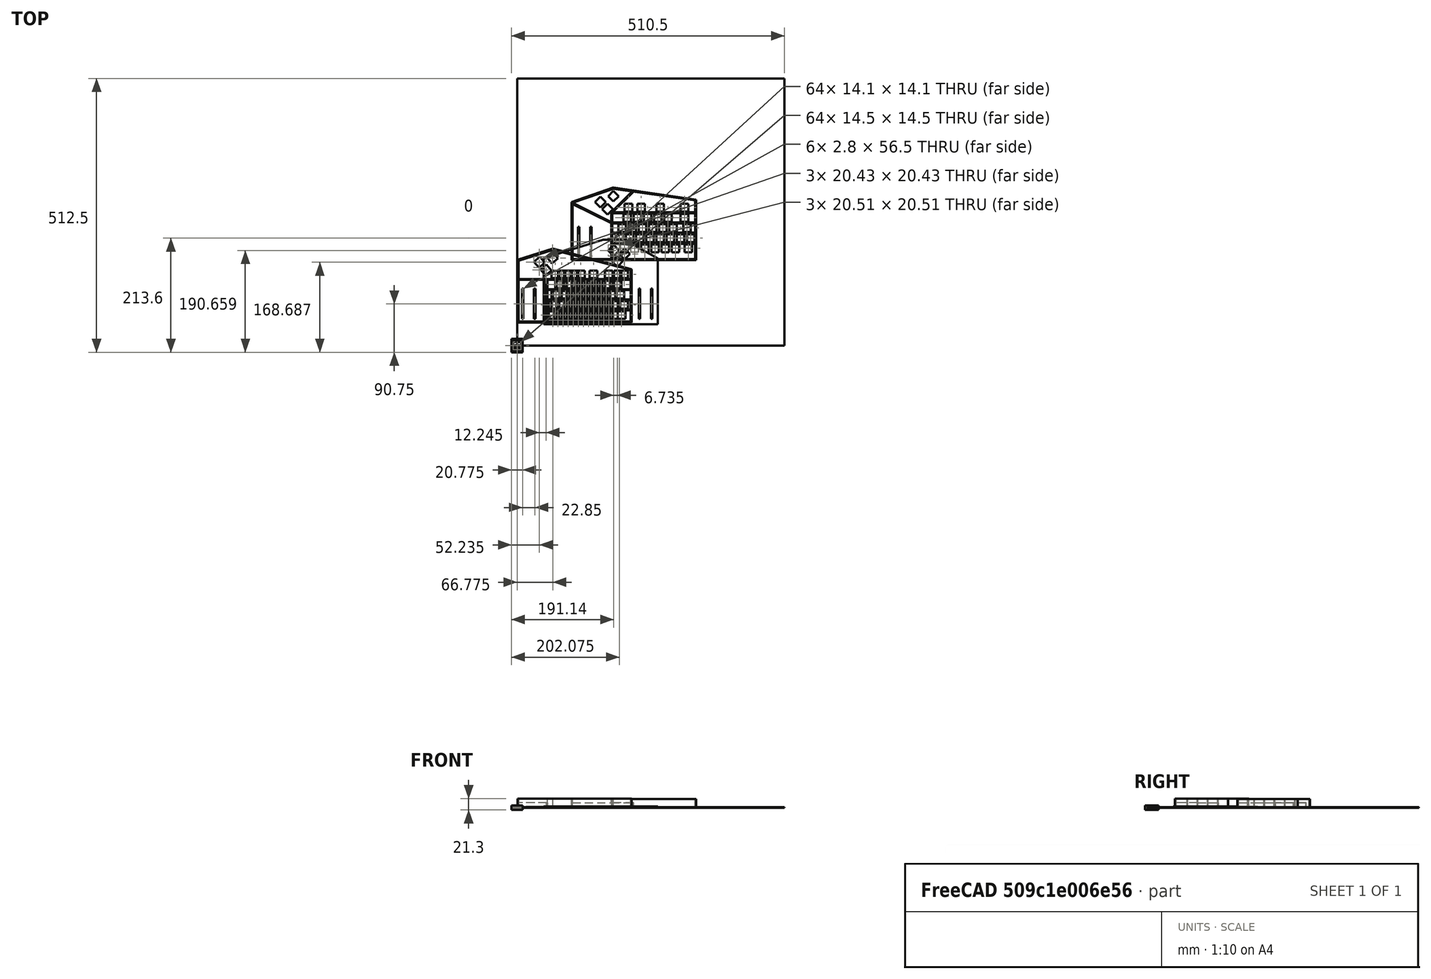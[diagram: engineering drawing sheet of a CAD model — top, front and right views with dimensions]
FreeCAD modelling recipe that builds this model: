
FCSTD DOCUMENT  (FreeCAD 0.22R35869 (Git))
Label: keyboard
License: All rights reserved
LicenseURL: http://en.wikipedia.org/wiki/All_rights_reserved
objects: PartDesign::Pad×30, Sketcher::SketchObject×29, PartDesign::Pocket×23, PartDesign::CoordinateSystem×11, PartDesign::Body×7, Part::Feature×7, App::Part×4, App::DocumentObjectGroup×3, App::Link×3, Mesh::Feature×3, Part::Refine×3, PartDesign::FeatureBase×3, PartDesign::Chamfer×2, PartDesign::Fillet×2, PartDesign::LinearPattern×2, App::FeaturePython×1, Spreadsheet::Sheet×1
note: 176 computed .brp shape members not serialized (recipe doc carries the construction recipe); baked Part::Feature solids carry a one-line shape summary decoded from their .brp

FEATURE [Sketcher::SketchObject] Sketch
  FullyConstrained = true
  MapMode = 5
  Support = -> [XY_Plane001]
  sketch-geometry (8):
    g0: LineSegment StartX=-7.5 StartY=7.5 StartZ=0 EndX=7.5 EndY=7.5 EndZ=0
    g1: LineSegment StartX=7.5 StartY=7.5 StartZ=0 EndX=7.5 EndY=-7.5 EndZ=0
    g2: LineSegment StartX=7.5 StartY=-7.5 StartZ=0 EndX=-7.5 EndY=-7.5 EndZ=0
    g3: LineSegment StartX=-7.5 StartY=-7.5 StartZ=0 EndX=-7.5 EndY=7.5 EndZ=0
    g4: LineSegment StartX=-10.5 StartY=10.5 StartZ=0 EndX=10.5 EndY=10.5 EndZ=0
    g5: LineSegment StartX=10.5 StartY=10.5 StartZ=0 EndX=10.5 EndY=-10.5 EndZ=0
    g6: LineSegment StartX=10.5 StartY=-10.5 StartZ=0 EndX=-10.5 EndY=-10.5 EndZ=0
    g7: LineSegment StartX=-10.5 StartY=-10.5 StartZ=0 EndX=-10.5 EndY=10.5 EndZ=0
  constraints (20):
    c: Coincident(g0,g1)
    c: Coincident(g1,g2)
    c: Coincident(g2,g3)
    c: Coincident(g3,g0)
    c: Horizontal(g2)
    c: Vertical(g1)
    c: Symmetric(g0,g0,g-2)
    c: Symmetric(g0,g2,g-1)
    c: Equal(g0,g3)
    c: DistanceX(g0,g0) = 15
    c: Coincident(g4,g5)
    c: Coincident(g5,g6)
    c: Coincident(g6,g7)
    c: Coincident(g7,g4)
    c: Horizontal(g6)
    c: Vertical(g5)
    c: Symmetric(g4,g4,g-2)
    c: Symmetric(g4,g6,g-1)
    c: Equal(g4,g7)
    c: DistanceX(g4,g0) = 3
FEATURE [PartDesign::Pad] Pad
  Direction = (0,0,1)
  Length = 2.5
  Length2 = 10
  Profile = -> Sketch
  ReferenceAxis = -> Sketch [N_Axis]
  Type = 0
FEATURE [Sketcher::SketchObject] Sketch001
  ExternalGeometry = -> [Pad]
  FullyConstrained = true
  MapMode = 5
  Placement = pos=(0,0,0) rot=(1,0,0;3.14159rad)
  Support = -> [Pad]
  expr: Constraints[11] = 4.15 / 2
  sketch-geometry (5):
    g0: LineSegment StartX=-10.5 StartY=10.5 StartZ=0 EndX=10.5 EndY=10.5 EndZ=0
    g1: LineSegment StartX=10.5 StartY=10.5 StartZ=0 EndX=10.5 EndY=-10.5 EndZ=0
    g2: LineSegment StartX=10.5 StartY=-10.5 StartZ=0 EndX=-10.5 EndY=-10.5 EndZ=0
    g3: LineSegment StartX=-10.5 StartY=-10.5 StartZ=0 EndX=-10.5 EndY=10.5 EndZ=0
    g4: Circle CenterX=0 CenterY=0 CenterZ=0 NormalX=0 NormalY=0 NormalZ=1 AngleXU=0 Radius=2.075
  constraints (12):
    c: Coincident(g0,g1)
    c: Coincident(g1,g2)
    c: Coincident(g2,g3)
    c: Coincident(g3,g0)
    c: Horizontal(g0)
    c: Horizontal(g2)
    c: Vertical(g1)
    c: Vertical(g3)
    c: Coincident(g0,g-3)
    c: Coincident(g1,g-4)
    c: Coincident(g4,g-1)
    c: Radius(g4) = 2.075
FEATURE [PartDesign::Pad] Pad001
  BaseFeature = -> Pad
  Direction = (0,0,-1)
  Length = 4
  Length2 = 10
  Profile = -> Sketch001
  ReferenceAxis = -> Sketch001 [N_Axis]
  Type = 0
FEATURE [Sketcher::SketchObject] Sketch002
  ExternalGeometry = -> [Pad001]
  FullyConstrained = true
  MapMode = 5
  Placement = pos=(0,0,2.5) rot=(0,0,1;0rad)
  Support = -> [Pad001]
  sketch-geometry (8):
    g0: LineSegment StartX=-10.5 StartY=10.5 StartZ=0 EndX=10.5 EndY=10.5 EndZ=0
    g1: LineSegment StartX=10.5 StartY=10.5 StartZ=0 EndX=10.5 EndY=-10.5 EndZ=0
    g2: LineSegment StartX=10.5 StartY=-10.5 StartZ=0 EndX=-10.5 EndY=-10.5 EndZ=0
    g3: LineSegment StartX=-10.5 StartY=-10.5 StartZ=0 EndX=-10.5 EndY=10.5 EndZ=0
    g4: LineSegment StartX=-7.25 StartY=7.25 StartZ=0 EndX=7.25 EndY=7.25 EndZ=0
    g5: LineSegment StartX=7.25 StartY=7.25 StartZ=0 EndX=7.25 EndY=-7.25 EndZ=0
    g6: LineSegment StartX=7.25 StartY=-7.25 StartZ=0 EndX=-7.25 EndY=-7.25 EndZ=0
    g7: LineSegment StartX=-7.25 StartY=-7.25 StartZ=0 EndX=-7.25 EndY=7.25 EndZ=0
  constraints (20):
    c: Coincident(g0,g1)
    c: Coincident(g1,g2)
    c: Coincident(g2,g3)
    c: Coincident(g3,g0)
    c: Horizontal(g0)
    c: Horizontal(g2)
    c: Vertical(g1)
    c: Vertical(g3)
    c: Coincident(g0,g-3)
    c: Coincident(g1,g-4)
    c: Coincident(g4,g5)
    c: Coincident(g5,g6)
    c: Coincident(g6,g7)
    c: Coincident(g7,g4)
    c: Horizontal(g6)
    c: Vertical(g5)
    c: Symmetric(g4,g4,g-2)
    c: Symmetric(g4,g6,g-1)
    c: DistanceX(g4,g4) = 14.5
    c: Equal(g7,g4)
FEATURE [PartDesign::Pad] Pad002
  BaseFeature = -> Pad001
  Direction = (0,0,1)
  Length = 2.3
  Length2 = 10
  Profile = -> Sketch002
  ReferenceAxis = -> Sketch002 [N_Axis]
  Type = 0
FEATURE [PartDesign::Chamfer] Chamfer
  Angle = 45
  Base = -> Pad002 [Edge19,Edge23,Edge11,Edge12]
  BaseFeature = -> Pad002
  ChamferType = 0
  FlipDirection = false
  Size = 3
  Size2 = 1
  SupportTransform = false
  UseAllEdges = false
FEATURE [Sketcher::SketchObject] Sketch003
  FullyConstrained = true
  MapMode = 5
  Placement = pos=(0,0,-4) rot=(1,0,0;3.14159rad)
  Support = -> [Chamfer]
  sketch-geometry (2):
    g0: Circle CenterX=4 CenterY=2.85 CenterZ=0 NormalX=0 NormalY=0 NormalZ=1 AngleXU=0 Radius=0.75
    g1: Circle CenterX=-2.9 CenterY=5 CenterZ=0 NormalX=0 NormalY=0 NormalZ=1 AngleXU=0 Radius=0.75
  constraints (6):
    c: DistanceX(g-1,g0) = 4
    c: DistanceY(g-1,g0) = 2.85
    c: Radius(g0) = 0.75
    c: DistanceX(g1,g-1) = 2.9
    c: DistanceY(g-1,g1) = 5
    c: Equal(g1,g0)
FEATURE [PartDesign::Pocket] Pocket
  BaseFeature = -> Chamfer
  Direction = (0,0,1)
  Length = 5
  Length2 = 5
  Profile = -> Sketch003
  ReferenceAxis = -> Sketch003 [N_Axis]
  Type = 1
FEATURE [PartDesign::Chamfer] Chamfer001
  Angle = 45
  Base = -> Pocket [Edge27,Edge26]
  BaseFeature = -> Pocket
  ChamferType = 1
  FlipDirection = false
  Size = 1.8
  Size2 = 3.999
  SupportTransform = false
  UseAllEdges = false
FEATURE [PartDesign::Body] Body
  Group = -> [Sketch,Pad,Sketch001,Pad001,Sketch002,Pad002,Chamfer,Sketch003,Pocket,Chamfer001]
  Origin = -> Origin001
  Tip = -> Chamfer001
FEATURE [Sketcher::SketchObject] Sketch004
  FullyConstrained = true
  MapMode = 5
  Support = -> [XY_Plane002]
  sketch-geometry (8):
    g0: LineSegment StartX=-7.5 StartY=7.5 StartZ=0 EndX=7.5 EndY=7.5 EndZ=0
    g1: LineSegment StartX=7.5 StartY=7.5 StartZ=0 EndX=7.5 EndY=-7.5 EndZ=0
    g2: LineSegment StartX=7.5 StartY=-7.5 StartZ=0 EndX=-7.5 EndY=-7.5 EndZ=0
    g3: LineSegment StartX=-7.5 StartY=-7.5 StartZ=0 EndX=-7.5 EndY=7.5 EndZ=0
    g4: LineSegment StartX=-10.5 StartY=10.5 StartZ=0 EndX=10.5 EndY=10.5 EndZ=0
    g5: LineSegment StartX=10.5 StartY=10.5 StartZ=0 EndX=10.5 EndY=-10.5 EndZ=0
    g6: LineSegment StartX=10.5 StartY=-10.5 StartZ=0 EndX=-10.5 EndY=-10.5 EndZ=0
    g7: LineSegment StartX=-10.5 StartY=-10.5 StartZ=0 EndX=-10.5 EndY=10.5 EndZ=0
  constraints (20):
    c: Coincident(g0,g1)
    c: Coincident(g1,g2)
    c: Coincident(g2,g3)
    c: Coincident(g3,g0)
    c: Horizontal(g2)
    c: Vertical(g1)
    c: Symmetric(g0,g0,g-2)
    c: Symmetric(g0,g2,g-1)
    c: Equal(g0,g3)
    c: DistanceX(g0,g0) = 15
    c: Coincident(g4,g5)
    c: Coincident(g5,g6)
    c: Coincident(g6,g7)
    c: Coincident(g7,g4)
    c: Horizontal(g6)
    c: Vertical(g5)
    c: Symmetric(g4,g4,g-2)
    c: Symmetric(g4,g6,g-1)
    c: Equal(g4,g7)
    c: DistanceX(g4,g0) = 3
FEATURE [PartDesign::Pad] Pad003
  Direction = (0,0,1)
  Length = 2.5
  Length2 = 10
  Profile = -> Sketch004
  ReferenceAxis = -> Sketch004 [N_Axis]
  Type = 0
FEATURE [Sketcher::SketchObject] Sketch005
  ExternalGeometry = -> [Pad003]
  FullyConstrained = true
  MapMode = 5
  Placement = pos=(0,0,0) rot=(1,0,0;3.14159rad)
  Support = -> [Pad003]
  expr: Constraints[11] = 4.15 / 2
  sketch-geometry (5):
    g0: LineSegment StartX=-10.5 StartY=10.5 StartZ=0 EndX=10.5 EndY=10.5 EndZ=0
    g1: LineSegment StartX=10.5 StartY=10.5 StartZ=0 EndX=10.5 EndY=-10.5 EndZ=0
    g2: LineSegment StartX=10.5 StartY=-10.5 StartZ=0 EndX=-10.5 EndY=-10.5 EndZ=0
    g3: LineSegment StartX=-10.5 StartY=-10.5 StartZ=0 EndX=-10.5 EndY=10.5 EndZ=0
    g4: Circle CenterX=0 CenterY=0 CenterZ=0 NormalX=0 NormalY=0 NormalZ=1 AngleXU=0 Radius=2.075
  constraints (12):
    c: Coincident(g0,g1)
    c: Coincident(g1,g2)
    c: Coincident(g2,g3)
    c: Coincident(g3,g0)
    c: Horizontal(g0)
    c: Horizontal(g2)
    c: Vertical(g1)
    c: Vertical(g3)
    c: Coincident(g0,g-3)
    c: Coincident(g1,g-4)
    c: Coincident(g4,g-1)
    c: Radius(g4) = 2.075
FEATURE [PartDesign::Pad] Pad004
  BaseFeature = -> Pad003
  Direction = (0,0,-1)
  Length = 4
  Length2 = 10
  Profile = -> Sketch005
  ReferenceAxis = -> Sketch005 [N_Axis]
  Type = 0
FEATURE [Sketcher::SketchObject] Sketch006
  ExternalGeometry = -> [Pad004]
  FullyConstrained = true
  MapMode = 5
  Placement = pos=(0,0,2.5) rot=(0,0,1;0rad)
  Support = -> [Pad004]
  sketch-geometry (8):
    g0: LineSegment StartX=-10.5 StartY=10.5 StartZ=0 EndX=10.5 EndY=10.5 EndZ=0
    g1: LineSegment StartX=10.5 StartY=10.5 StartZ=0 EndX=10.5 EndY=-10.5 EndZ=0
    g2: LineSegment StartX=10.5 StartY=-10.5 StartZ=0 EndX=-10.5 EndY=-10.5 EndZ=0
    g3: LineSegment StartX=-10.5 StartY=-10.5 StartZ=0 EndX=-10.5 EndY=10.5 EndZ=0
    g4: LineSegment StartX=-7.25 StartY=7.25 StartZ=0 EndX=7.25 EndY=7.25 EndZ=0
    g5: LineSegment StartX=7.25 StartY=7.25 StartZ=0 EndX=7.25 EndY=-7.25 EndZ=0
    g6: LineSegment StartX=7.25 StartY=-7.25 StartZ=0 EndX=-7.25 EndY=-7.25 EndZ=0
    g7: LineSegment StartX=-7.25 StartY=-7.25 StartZ=0 EndX=-7.25 EndY=7.25 EndZ=0
  constraints (20):
    c: Coincident(g0,g1)
    c: Coincident(g1,g2)
    c: Coincident(g2,g3)
    c: Coincident(g3,g0)
    c: Horizontal(g0)
    c: Horizontal(g2)
    c: Vertical(g1)
    c: Vertical(g3)
    c: Coincident(g0,g-3)
    c: Coincident(g1,g-4)
    c: Coincident(g4,g5)
    c: Coincident(g5,g6)
    c: Coincident(g6,g7)
    c: Coincident(g7,g4)
    c: Horizontal(g6)
    c: Vertical(g5)
    c: Symmetric(g4,g4,g-2)
    c: Symmetric(g4,g6,g-1)
    c: DistanceX(g4,g4) = 14.5
    c: Equal(g7,g4)
FEATURE [PartDesign::Pad] Pad005
  BaseFeature = -> Pad004
  Direction = (0,0,1)
  Length = 2.3
  Length2 = 10
  Profile = -> Sketch006
  ReferenceAxis = -> Sketch006 [N_Axis]
  Type = 0
FEATURE [Sketcher::SketchObject] Sketch007
  ExternalGeometry = -> [Pad005]
  FullyConstrained = true
  MapMode = 5
  Placement = pos=(0,0,-4) rot=(1,0,0;3.14159rad)
  Support = -> [Pad005]
  sketch-geometry (22):
    g0: LineSegment StartX=-7.5 StartY=6.5 StartZ=0 EndX=-2 EndY=6.5 EndZ=0
    g1: LineSegment StartX=-2 StartY=6.5 StartZ=0 EndX=-2 EndY=3.5 EndZ=0
    g2: LineSegment StartX=-2 StartY=3.5 StartZ=0 EndX=-7.5 EndY=3.5 EndZ=0
    g3: LineSegment StartX=-7.5 StartY=3.5 StartZ=0 EndX=-7.5 EndY=6.5 EndZ=0
    g4: LineSegment StartX=3 StartY=4.35 StartZ=0 EndX=7.5 EndY=4.35 EndZ=0
    g5: LineSegment StartX=7.5 StartY=4.35 StartZ=0 EndX=7.5 EndY=1.35 EndZ=0
    g6: LineSegment StartX=7.5 StartY=1.35 StartZ=0 EndX=3 EndY=1.35 EndZ=0
    g7: LineSegment StartX=3 StartY=1.35 StartZ=0 EndX=3 EndY=4.35 EndZ=0
    g8: Circle CenterX=-2.9 CenterY=5 CenterZ=0 NormalX=0 NormalY=0 NormalZ=1 AngleXU=0 Radius=0.75
    g9: Circle CenterX=4 CenterY=2.85 CenterZ=0 NormalX=0 NormalY=0 NormalZ=1 AngleXU=0 Radius=0.75
    g10: LineSegment StartX=-2.9 StartY=5 StartZ=0 EndX=-7.5 EndY=5 EndZ=0
    g11: LineSegment StartX=-7.5 StartY=5 StartZ=0 EndX=-7.5 EndY=6.5 EndZ=0
    g12: LineSegment StartX=-7.5 StartY=5 StartZ=0 EndX=-7.5 EndY=3.5 EndZ=0
    g13: LineSegment StartX=4 StartY=2.85 StartZ=0 EndX=7.5 EndY=2.85 EndZ=0
    g14: LineSegment StartX=7.5 StartY=2.85 StartZ=0 EndX=7.5 EndY=1.35 EndZ=0
    g15: LineSegment StartX=7.5 StartY=2.85 StartZ=0 EndX=7.5 EndY=4.35 EndZ=0
    g16: LineSegment StartX=3 StartY=4.35 StartZ=0 EndX=3.8 EndY=3.57284 EndZ=0
    g17: LineSegment StartX=3 StartY=1.35 StartZ=0 EndX=3.8 EndY=2.12716 EndZ=0
    g18: ArcOfCircle CenterX=4 CenterY=2.85 CenterZ=0 NormalX=0 NormalY=0 NormalZ=1 AngleXU=0 Radius=0.75 StartAngle=1.84073 EndAngle=4.44246
    g19: LineSegment StartX=-2 StartY=6.5 StartZ=0 EndX=-2.7 EndY=5.72284 EndZ=0
    g20: LineSegment StartX=-2 StartY=3.5 StartZ=0 EndX=-2.7 EndY=4.27716 EndZ=0
    g21: ArcOfCircle CenterX=-2.9 CenterY=5 CenterZ=0 NormalX=0 NormalY=0 NormalZ=1 AngleXU=0 Radius=0.75 StartAngle=4.98232 EndAngle=7.58405
  constraints (60):
    c: Coincident(g0,g1)
    c: Coincident(g1,g2)
    c: Coincident(g2,g3)
    c: Coincident(g3,g0)
    c: Horizontal(g0)
    c: Horizontal(g2)
    c: Vertical(g1)
    c: Vertical(g3)
    c: Coincident(g4,g5)
    c: Coincident(g5,g6)
    c: Coincident(g6,g7)
    c: Coincident(g7,g4)
    c: Horizontal(g4)
    c: Horizontal(g6)
    c: Vertical(g5)
    c: Vertical(g7)
    c: PointOnObject(g4,g-4)
    c: PointOnObject(g0,g-3)
    c: DistanceY(g-1,g9) = 2.85
    c: DistanceX(g-1,g9) = 4
    c: Radius(g9) = 0.75
    c: DistanceY(g-1,g8) = 5
    c: DistanceX(g8,g-1) = 2.9
    c: Radius(g8) = 0.75
    c: Coincident(g10,g8)
    c: PointOnObject(g10,g-3)
    c: Coincident(g11,g10)
    c: Equal(g12,g11)
    c: Coincident(g12,g10)
    c: Horizontal(g10)
    c: Coincident(g12,g2)
    c: Coincident(g11,g0)
    c: Coincident(g13,g9)
    c: PointOnObject(g13,g-4)
    c: Coincident(g14,g13)
    c: Coincident(g15,g13)
    c: Equal(g15,g14)
    c: Horizontal(g13)
    c: Coincident(g15,g4)
    c: Coincident(g14,g5)
    c: DistanceX(g6,g5) = 4.5
    c: DistanceX(g2,g2) = 5.5
    c: DistanceY(g1,g1) = 3
    c: Coincident(g16,g4)
    c: Coincident(g17,g6)
    c: Coincident(g18,g9)
    c: Coincident(g18,g16)
    c: Coincident(g18,g17)
    c: Equal(g18,g9)
    c: DistanceX(g17,g18) = 0.2
    c: Equal(g16,g17)
    c: Coincident(g19,g0)
    c: PointOnObject(g19,g8)
    c: Coincident(g20,g2)
    c: Coincident(g21,g8)
    c: Coincident(g21,g19)
    c: Coincident(g21,g20)
    c: Equal(g19,g20)
    c: DistanceX(g21,g20) = 0.2
    c: Equal(g1,g7)
FEATURE [PartDesign::Pocket] Pocket001
  BaseFeature = -> Pad005
  Direction = (0,0,1)
  Length = 0
  Length2 = 5
  Profile = -> Sketch007
  ReferenceAxis = -> Sketch007 [N_Axis]
  Type = 3
  UpToFace = -> Pad005 [Face20]
FEATURE [PartDesign::Fillet] Fillet
  Base = -> Pocket001 [Edge65,Edge68,Edge49,Edge53]
  BaseFeature = -> Pocket001
  Radius = 1
  SupportTransform = false
  UseAllEdges = false
FEATURE [Sketcher::SketchObject] Sketch008
  ExternalGeometry = -> [Fillet]
  FullyConstrained = true
  MapMode = 5
  Placement = pos=(0,0,4.8) rot=(0,0,1;0rad)
  Support = -> [Fillet]
  sketch-geometry (4):
    g0: LineSegment StartX=-10.5 StartY=0 StartZ=0 EndX=10.5 EndY=0 EndZ=0
    g1: LineSegment StartX=10.5 StartY=0 StartZ=0 EndX=10.5 EndY=-6.5 EndZ=0
    g2: LineSegment StartX=10.5 StartY=-6.5 StartZ=0 EndX=-10.5 EndY=-6.5 EndZ=0
    g3: LineSegment StartX=-10.5 StartY=-6.5 StartZ=0 EndX=-10.5 EndY=0 EndZ=0
  constraints (11):
    c: Coincident(g0,g1)
    c: Coincident(g1,g2)
    c: Coincident(g2,g3)
    c: Coincident(g3,g0)
    c: Horizontal(g2)
    c: Vertical(g1)
    c: Vertical(g3)
    c: PointOnObject(g0,g-1)
    c: PointOnObject(g2,g-3)
    c: Symmetric(g0,g0,g-2)
    c: PointOnObject(g2,g-4)
FEATURE [PartDesign::Pocket] Pocket002
  BaseFeature = -> Fillet
  Direction = (0,0,-1)
  Length = 0
  Length2 = 5
  Profile = -> Sketch008
  ReferenceAxis = -> Sketch008 [N_Axis]
  Type = 3
  UpToFace = -> Fillet [Face23]
FEATURE [PartDesign::Pad] Pad006
  BaseFeature = -> Pocket002
  Direction = (0,-1,0)
  Length = 2
  Length2 = 10
  Profile = -> Pocket002 [Face10,Face26,Face39]
  Type = 0
FEATURE [PartDesign::Pad] Pad007
  BaseFeature = -> Pad006
  Direction = (0,1,0)
  Length = 2
  Length2 = 10
  Profile = -> Pad006 [Face13,Face34,Face50]
  Type = 0
FEATURE [PartDesign::CoordinateSystem] LCS_Origin
  AttacherType = Attacher::AttachEngine3D
  MapMode = 2
  Support = -> [X_Axis006]
FEATURE [App::DocumentObjectGroup] Constraints
FEATURE [App::FeaturePython] Variables  # WARN: FeaturePython — macro-defined, semantics opaque (R4)
  Type = App::PropertyContainer
FEATURE [App::DocumentObjectGroup] Configurations
FEATURE [PartDesign::CoordinateSystem] LCS_0
  AttacherType = Attacher::AttachEngine3D
  MapMode = 2
  Support = -> [X_Axis007]
FEATURE [Sketcher::SketchObject] Sketch013
  FullyConstrained = true
  MapMode = 5
  Support = -> [XY_Plane008]
  sketch-geometry (6):
    g0: ArcOfCircle CenterX=-0.866025 CenterY=0 CenterZ=0 NormalX=0 NormalY=0 NormalZ=1 AngleXU=0 Radius=1 StartAngle=5.75959 EndAngle=6.80678
    g1: LineSegment StartX=0 StartY=0.5 StartZ=0 EndX=0 EndY=1 EndZ=0
    g2: LineSegment StartX=0 StartY=1 StartZ=0 EndX=1 EndY=1 EndZ=0
    g3: LineSegment StartX=1 StartY=1 StartZ=0 EndX=1 EndY=-1 EndZ=0
    g4: LineSegment StartX=1 StartY=-1 StartZ=0 EndX=0 EndY=-1 EndZ=0
    g5: LineSegment StartX=0 StartY=-1 StartZ=0 EndX=2e-16 EndY=-0.5 EndZ=0
  constraints (19):
    c: PointOnObject(g0,g-1)
    c: PointOnObject(g0,g-2)
    c: PointOnObject(g0,g-2)
    c: Coincident(g1,g2)
    c: Horizontal(g2)
    c: Coincident(g2,g3)
    c: Coincident(g3,g4)
    c: PointOnObject(g4,g-2)
    c: Horizontal(g4)
    c: Coincident(g4,g5)
    c: Coincident(g5,g0)
    c: PointOnObject(g1,g-2)
    c: Vertical(g3)
    c: DistanceY(g3,g3) = 2
    c: Radius(g0) = 1
    c: Coincident(g1,g0)
    c: Equal(g1,g5)
    c: DistanceY(g0,g0) = 1
    c: DistanceX(g2,g2) = 1
FEATURE [PartDesign::Pad] Pad011
  Direction = (0,0,1)
  Length = 4
  Length2 = 10
  Profile = -> Sketch013
  ReferenceAxis = -> Sketch013 [N_Axis]
  Reversed = true
  Type = 0
FEATURE [PartDesign::CoordinateSystem] Local_CS
  AttacherType = Attacher::AttachEngine3D
  MapMode = 45
  Placement = pos=(3.31163,-2.85,0) rot=(0,0.707107,0.707107;3.14159rad)
  Support = -> [Pad007]
FEATURE [PartDesign::CoordinateSystem] Local_CS001
  AttacherType = Attacher::AttachEngine3D
  MapMode = 45
  Placement = pos=(-2.22398,-5,0) rot=(0,0.707107,0.707107;3.14159rad)
  Support = -> [Pad007]
FEATURE [PartDesign::Body] Body001
  Group = -> [Sketch004,Pad003,Sketch005,Pad004,Sketch006,Pad005,Sketch007,Pocket001,Fillet,Sketch008,Pocket002,Pad006,Pad007,Local_CS,Local_CS001]
  Origin = -> Origin002
  Tip = -> Pad007
FEATURE [Sketcher::SketchObject] Sketch014
  ExternalGeometry = -> [Pad011]
  FullyConstrained = true
  MapMode = 5
  Support = -> [XY_Plane008]
  sketch-geometry (21):
    g0: LineSegment StartX=1 StartY=1 StartZ=0 EndX=1.66667 EndY=-0.8 EndZ=0
    g1: LineSegment StartX=1.66667 StartY=-0.8 StartZ=0 EndX=2.33333 EndY=1 EndZ=0
    g2: LineSegment StartX=2.33333 StartY=1 StartZ=0 EndX=3 EndY=-0.8 EndZ=0
    g3: LineSegment StartX=3 StartY=-0.8 StartZ=0 EndX=3.66667 EndY=1 EndZ=0
    g4: LineSegment StartX=3.66667 StartY=1 StartZ=0 EndX=4.33333 EndY=-0.8 EndZ=0
    g5: LineSegment StartX=4.33333 StartY=-0.8 StartZ=0 EndX=5 EndY=1 EndZ=0
    g6: LineSegment StartX=1 StartY=1 StartZ=0 EndX=5 EndY=1 EndZ=0
    g7: LineSegment StartX=1 StartY=-1 StartZ=0 EndX=4.33333 EndY=-1 EndZ=0
    g8: LineSegment StartX=1 StartY=0.8 StartZ=0 EndX=1.66667 EndY=-1 EndZ=0
    g9: LineSegment StartX=1.66667 StartY=-1 StartZ=0 EndX=2.33333 EndY=0.8 EndZ=0
    g10: LineSegment StartX=2.33333 StartY=0.8 StartZ=0 EndX=3 EndY=-1 EndZ=0
    g11: LineSegment StartX=3 StartY=-1 StartZ=0 EndX=3.66667 EndY=0.8 EndZ=0
    g12: LineSegment StartX=3.66667 StartY=0.8 StartZ=0 EndX=4.33333 EndY=-1 EndZ=0
    g13: LineSegment StartX=4.33333 StartY=-1 StartZ=0 EndX=5 EndY=0.8 EndZ=0
    g14: LineSegment StartX=1.66667 StartY=-0.8 StartZ=0 EndX=1.66667 EndY=-1 EndZ=0
    g15: LineSegment StartX=3 StartY=-0.8 StartZ=0 EndX=3 EndY=-1 EndZ=0
    g16: LineSegment StartX=2.33333 StartY=0.8 StartZ=0 EndX=2.33333 EndY=1 EndZ=0
    g17: LineSegment StartX=3.66667 StartY=0.8 StartZ=0 EndX=3.66667 EndY=1 EndZ=0
    g18: LineSegment StartX=5 StartY=0.8 StartZ=0 EndX=5 EndY=1 EndZ=0
    g19: LineSegment StartX=4.33333 StartY=-0.8 StartZ=0 EndX=4.33333 EndY=-1 EndZ=0
    g20: LineSegment StartX=1 StartY=0.8 StartZ=0 EndX=1 EndY=1 EndZ=0
  constraints (55):
    c: Coincident(g-3,g0)
    c: Coincident(g0,g1)
    c: Coincident(g1,g2)
    c: Coincident(g2,g3)
    c: Coincident(g3,g4)
    c: Coincident(g6,g0)
    c: Coincident(g6,g5)
    c: Coincident(g7,g-3)
    c: Horizontal(g7)
    c: Horizontal(g6)
    c: PointOnObject(g3,g6)
    c: PointOnObject(g1,g6)
    c: Coincident(g5,g4)
    c: PointOnObject(g8,g-3)
    c: PointOnObject(g8,g7)
    c: Coincident(g8,g9)
    c: Coincident(g9,g10)
    c: PointOnObject(g10,g7)
    c: Coincident(g10,g11)
    c: Coincident(g11,g12)
    c: Coincident(g12,g7)
    c: Coincident(g12,g13)
    c: Coincident(g14,g0)
    c: Coincident(g14,g8)
    c: Coincident(g15,g2)
    c: Coincident(g15,g10)
    c: Coincident(g16,g9)
    c: Coincident(g16,g1)
    c: Coincident(g17,g11)
    c: Coincident(g17,g3)
    c: Vertical(g17)
    c: Coincident(g18,g13)
    c: Coincident(g18,g5)
    c: Coincident(g19,g4)
    c: Coincident(g19,g12)
    c: Equal(g14,g16)
    c: Equal(g16,g15)
    c: Equal(g15,g17)
    c: Equal(g17,g19)
    c: Equal(g19,g18)
    c: Vertical(g14)
    c: Vertical(g16)
    c: Vertical(g15)
    c: Vertical(g18)
    c: Vertical(g19)
    c: Equal(g0,g1)
    c: Equal(g2,g3)
    c: Equal(g3,g4)
    c: Equal(g4,g5)
    c: Equal(g5,g8)
    c: Equal(g8,g9)
    c: Coincident(g20,g8)
    c: Coincident(g20,g0)
    c: DistanceY(g18,g18) = 0.2
    c: DistanceX(g6,g6) = 4
FEATURE [PartDesign::Pad] Pad012
  BaseFeature = -> Pad011
  Direction = (0,0,1)
  Length = 4
  Length2 = 10
  Profile = -> Sketch014
  ReferenceAxis = -> Sketch014 [N_Axis]
  Reversed = true
  Type = 0
FEATURE [PartDesign::CoordinateSystem] LCS_0002
  AttacherType = Attacher::AttachEngine3D
  MapMode = 2
  Support = -> [X_Axis009]
FEATURE [Sketcher::SketchObject] Sketch015
  FullyConstrained = true
  MapMode = 5
  Support = -> [XY_Plane010]
  sketch-geometry (8):
    g0: LineSegment StartX=-7.5 StartY=7.5 StartZ=0 EndX=7.5 EndY=7.5 EndZ=0
    g1: LineSegment StartX=7.5 StartY=7.5 StartZ=0 EndX=7.5 EndY=-7.5 EndZ=0
    g2: LineSegment StartX=7.5 StartY=-7.5 StartZ=0 EndX=-7.5 EndY=-7.5 EndZ=0
    g3: LineSegment StartX=-7.5 StartY=-7.5 StartZ=0 EndX=-7.5 EndY=7.5 EndZ=0
    g4: LineSegment StartX=-10.5 StartY=10.5 StartZ=0 EndX=10.5 EndY=10.5 EndZ=0
    g5: LineSegment StartX=10.5 StartY=10.5 StartZ=0 EndX=10.5 EndY=-10.5 EndZ=0
    g6: LineSegment StartX=10.5 StartY=-10.5 StartZ=0 EndX=-10.5 EndY=-10.5 EndZ=0
    g7: LineSegment StartX=-10.5 StartY=-10.5 StartZ=0 EndX=-10.5 EndY=10.5 EndZ=0
  constraints (20):
    c: Coincident(g0,g1)
    c: Coincident(g1,g2)
    c: Coincident(g2,g3)
    c: Coincident(g3,g0)
    c: Horizontal(g2)
    c: Vertical(g1)
    c: Symmetric(g0,g0,g-2)
    c: Symmetric(g0,g2,g-1)
    c: Equal(g0,g3)
    c: DistanceX(g0,g0) = 15
    c: Coincident(g4,g5)
    c: Coincident(g5,g6)
    c: Coincident(g6,g7)
    c: Coincident(g7,g4)
    c: Horizontal(g6)
    c: Vertical(g5)
    c: Symmetric(g4,g4,g-2)
    c: Symmetric(g4,g6,g-1)
    c: Equal(g4,g7)
    c: DistanceX(g4,g0) = 3
FEATURE [PartDesign::Pad] Pad013
  Direction = (0,0,1)
  Length = 2.5
  Length2 = 10
  Profile = -> Sketch015
  ReferenceAxis = -> Sketch015 [N_Axis]
  Type = 0
FEATURE [Sketcher::SketchObject] Sketch016
  ExternalGeometry = -> [Pad013]
  FullyConstrained = true
  MapMode = 5
  Placement = pos=(0,0,0) rot=(1,0,0;3.14159rad)
  Support = -> [Pad013]
  expr: Constraints[11] = 4.15 / 2
  sketch-geometry (5):
    g0: LineSegment StartX=-10.5 StartY=10.5 StartZ=0 EndX=10.5 EndY=10.5 EndZ=0
    g1: LineSegment StartX=10.5 StartY=10.5 StartZ=0 EndX=10.5 EndY=-10.5 EndZ=0
    g2: LineSegment StartX=10.5 StartY=-10.5 StartZ=0 EndX=-10.5 EndY=-10.5 EndZ=0
    g3: LineSegment StartX=-10.5 StartY=-10.5 StartZ=0 EndX=-10.5 EndY=10.5 EndZ=0
    g4: Circle CenterX=0 CenterY=0 CenterZ=0 NormalX=0 NormalY=0 NormalZ=1 AngleXU=0 Radius=2.075
  constraints (12):
    c: Coincident(g0,g1)
    c: Coincident(g1,g2)
    c: Coincident(g2,g3)
    c: Coincident(g3,g0)
    c: Horizontal(g0)
    c: Horizontal(g2)
    c: Vertical(g1)
    c: Vertical(g3)
    c: Coincident(g0,g-3)
    c: Coincident(g1,g-4)
    c: Coincident(g4,g-1)
    c: Radius(g4) = 2.075
FEATURE [PartDesign::Pad] Pad014
  BaseFeature = -> Pad013
  Direction = (0,0,-1)
  Length = 4
  Length2 = 10
  Profile = -> Sketch016
  ReferenceAxis = -> Sketch016 [N_Axis]
  Type = 0
FEATURE [Sketcher::SketchObject] Sketch017
  ExternalGeometry = -> [Pad014]
  FullyConstrained = true
  MapMode = 5
  Placement = pos=(0,0,2.5) rot=(0,0,1;0rad)
  Support = -> [Pad014]
  sketch-geometry (8):
    g0: LineSegment StartX=-10.5 StartY=10.5 StartZ=0 EndX=10.5 EndY=10.5 EndZ=0
    g1: LineSegment StartX=10.5 StartY=10.5 StartZ=0 EndX=10.5 EndY=-10.5 EndZ=0
    g2: LineSegment StartX=10.5 StartY=-10.5 StartZ=0 EndX=-10.5 EndY=-10.5 EndZ=0
    g3: LineSegment StartX=-10.5 StartY=-10.5 StartZ=0 EndX=-10.5 EndY=10.5 EndZ=0
    g4: LineSegment StartX=-7.25 StartY=7.25 StartZ=0 EndX=7.25 EndY=7.25 EndZ=0
    g5: LineSegment StartX=7.25 StartY=7.25 StartZ=0 EndX=7.25 EndY=-7.25 EndZ=0
    g6: LineSegment StartX=7.25 StartY=-7.25 StartZ=0 EndX=-7.25 EndY=-7.25 EndZ=0
    g7: LineSegment StartX=-7.25 StartY=-7.25 StartZ=0 EndX=-7.25 EndY=7.25 EndZ=0
  constraints (20):
    c: Coincident(g0,g1)
    c: Coincident(g1,g2)
    c: Coincident(g2,g3)
    c: Coincident(g3,g0)
    c: Horizontal(g0)
    c: Horizontal(g2)
    c: Vertical(g1)
    c: Vertical(g3)
    c: Coincident(g0,g-3)
    c: Coincident(g1,g-4)
    c: Coincident(g4,g5)
    c: Coincident(g5,g6)
    c: Coincident(g6,g7)
    c: Coincident(g7,g4)
    c: Horizontal(g6)
    c: Vertical(g5)
    c: Symmetric(g4,g4,g-2)
    c: Symmetric(g4,g6,g-1)
    c: DistanceX(g4,g4) = 14.5
    c: Equal(g7,g4)
FEATURE [PartDesign::Pad] Pad015
  BaseFeature = -> Pad014
  Direction = (0,0,1)
  Length = 2.3
  Length2 = 10
  Profile = -> Sketch017
  ReferenceAxis = -> Sketch017 [N_Axis]
  Type = 0
FEATURE [Sketcher::SketchObject] Sketch018
  ExternalGeometry = -> [Pad015]
  FullyConstrained = true
  MapMode = 5
  Placement = pos=(0,0,-4) rot=(1,0,0;3.14159rad)
  Support = -> [Pad015]
  sketch-geometry (22):
    g0: LineSegment StartX=-7.5 StartY=6.5 StartZ=0 EndX=-2 EndY=6.5 EndZ=0
    g1: LineSegment StartX=-2 StartY=6.5 StartZ=0 EndX=-2 EndY=3.5 EndZ=0
    g2: LineSegment StartX=-2 StartY=3.5 StartZ=0 EndX=-7.5 EndY=3.5 EndZ=0
    g3: LineSegment StartX=-7.5 StartY=3.5 StartZ=0 EndX=-7.5 EndY=6.5 EndZ=0
    g4: LineSegment StartX=3 StartY=4.35 StartZ=0 EndX=7.5 EndY=4.35 EndZ=0
    g5: LineSegment StartX=7.5 StartY=4.35 StartZ=0 EndX=7.5 EndY=1.35 EndZ=0
    g6: LineSegment StartX=7.5 StartY=1.35 StartZ=0 EndX=3 EndY=1.35 EndZ=0
    g7: LineSegment StartX=3 StartY=1.35 StartZ=0 EndX=3 EndY=4.35 EndZ=0
    g8: Circle CenterX=-2.9 CenterY=5 CenterZ=0 NormalX=0 NormalY=0 NormalZ=1 AngleXU=0 Radius=0.75
    g9: Circle CenterX=4 CenterY=2.85 CenterZ=0 NormalX=0 NormalY=0 NormalZ=1 AngleXU=0 Radius=0.75
    g10: LineSegment StartX=-2.9 StartY=5 StartZ=0 EndX=-7.5 EndY=5 EndZ=0
    g11: LineSegment StartX=-7.5 StartY=5 StartZ=0 EndX=-7.5 EndY=6.5 EndZ=0
    g12: LineSegment StartX=-7.5 StartY=5 StartZ=0 EndX=-7.5 EndY=3.5 EndZ=0
    g13: LineSegment StartX=4 StartY=2.85 StartZ=0 EndX=7.5 EndY=2.85 EndZ=0
    g14: LineSegment StartX=7.5 StartY=2.85 StartZ=0 EndX=7.5 EndY=1.35 EndZ=0
    g15: LineSegment StartX=7.5 StartY=2.85 StartZ=0 EndX=7.5 EndY=4.35 EndZ=0
    g16: LineSegment StartX=3 StartY=4.35 StartZ=0 EndX=3.8 EndY=3.57284 EndZ=0
    g17: LineSegment StartX=3 StartY=1.35 StartZ=0 EndX=3.8 EndY=2.12716 EndZ=0
    g18: ArcOfCircle CenterX=4 CenterY=2.85 CenterZ=0 NormalX=0 NormalY=0 NormalZ=1 AngleXU=0 Radius=0.75 StartAngle=1.84073 EndAngle=4.44246
    g19: LineSegment StartX=-2 StartY=6.5 StartZ=0 EndX=-2.7 EndY=5.72284 EndZ=0
    g20: LineSegment StartX=-2 StartY=3.5 StartZ=0 EndX=-2.7 EndY=4.27716 EndZ=0
    g21: ArcOfCircle CenterX=-2.9 CenterY=5 CenterZ=0 NormalX=0 NormalY=0 NormalZ=1 AngleXU=0 Radius=0.75 StartAngle=4.98232 EndAngle=7.58405
  constraints (60):
    c: Coincident(g0,g1)
    c: Coincident(g1,g2)
    c: Coincident(g2,g3)
    c: Coincident(g3,g0)
    c: Horizontal(g0)
    c: Horizontal(g2)
    c: Vertical(g1)
    c: Vertical(g3)
    c: Coincident(g4,g5)
    c: Coincident(g5,g6)
    c: Coincident(g6,g7)
    c: Coincident(g7,g4)
    c: Horizontal(g4)
    c: Horizontal(g6)
    c: Vertical(g5)
    c: Vertical(g7)
    c: PointOnObject(g4,g-4)
    c: PointOnObject(g0,g-3)
    c: DistanceY(g-1,g9) = 2.85
    c: DistanceX(g-1,g9) = 4
    c: Radius(g9) = 0.75
    c: DistanceY(g-1,g8) = 5
    c: DistanceX(g8,g-1) = 2.9
    c: Radius(g8) = 0.75
    c: Coincident(g10,g8)
    c: PointOnObject(g10,g-3)
    c: Coincident(g11,g10)
    c: Equal(g12,g11)
    c: Coincident(g12,g10)
    c: Horizontal(g10)
    c: Coincident(g12,g2)
    c: Coincident(g11,g0)
    c: Coincident(g13,g9)
    c: PointOnObject(g13,g-4)
    c: Coincident(g14,g13)
    c: Coincident(g15,g13)
    c: Equal(g15,g14)
    c: Horizontal(g13)
    c: Coincident(g15,g4)
    c: Coincident(g14,g5)
    c: DistanceX(g6,g5) = 4.5
    c: DistanceX(g2,g2) = 5.5
    c: DistanceY(g1,g1) = 3
    c: Coincident(g16,g4)
    c: Coincident(g17,g6)
    c: Coincident(g18,g9)
    c: Coincident(g18,g16)
    c: Coincident(g18,g17)
    c: Equal(g18,g9)
    c: DistanceX(g17,g18) = 0.2
    c: Equal(g16,g17)
    c: Coincident(g19,g0)
    c: PointOnObject(g19,g8)
    c: Coincident(g20,g2)
    c: Coincident(g21,g8)
    c: Coincident(g21,g19)
    c: Coincident(g21,g20)
    c: Equal(g19,g20)
    c: DistanceX(g21,g20) = 0.2
    c: Equal(g1,g7)
FEATURE [PartDesign::Pocket] Pocket003
  BaseFeature = -> Pad015
  Direction = (0,0,1)
  Length = 0
  Length2 = 5
  Profile = -> Sketch018
  ReferenceAxis = -> Sketch018 [N_Axis]
  Type = 3
  UpToFace = -> Pad015 [Face20]
FEATURE [PartDesign::Fillet] Fillet001
  Base = -> Pocket003 [Edge65,Edge68,Edge49,Edge53]
  BaseFeature = -> Pocket003
  Radius = 1
  SupportTransform = false
  UseAllEdges = false
FEATURE [Sketcher::SketchObject] Sketch019
  ExternalGeometry = -> [Fillet001]
  FullyConstrained = true
  MapMode = 5
  Placement = pos=(0,0,4.8) rot=(0,0,1;0rad)
  Support = -> [Fillet001]
  sketch-geometry (4):
    g0: LineSegment StartX=-10.5 StartY=0 StartZ=0 EndX=10.5 EndY=0 EndZ=0
    g1: LineSegment StartX=10.5 StartY=0 StartZ=0 EndX=10.5 EndY=-6.5 EndZ=0
    g2: LineSegment StartX=10.5 StartY=-6.5 StartZ=0 EndX=-10.5 EndY=-6.5 EndZ=0
    g3: LineSegment StartX=-10.5 StartY=-6.5 StartZ=0 EndX=-10.5 EndY=0 EndZ=0
  constraints (11):
    c: Coincident(g0,g1)
    c: Coincident(g1,g2)
    c: Coincident(g2,g3)
    c: Coincident(g3,g0)
    c: Horizontal(g2)
    c: Vertical(g1)
    c: Vertical(g3)
    c: PointOnObject(g0,g-1)
    c: PointOnObject(g2,g-3)
    c: Symmetric(g0,g0,g-2)
    c: PointOnObject(g2,g-4)
FEATURE [PartDesign::Pocket] Pocket004
  BaseFeature = -> Fillet001
  Direction = (0,0,-1)
  Length = 0
  Length2 = 5
  Profile = -> Sketch019
  ReferenceAxis = -> Sketch019 [N_Axis]
  Type = 3
  UpToFace = -> Fillet001 [Face23]
FEATURE [PartDesign::Pad] Pad016
  BaseFeature = -> Pocket004
  Direction = (0,-1,0)
  Length = 2
  Length2 = 10
  Profile = -> Pocket004 [Face10,Face26,Face39]
  Type = 0
FEATURE [PartDesign::Pad] Pad017
  BaseFeature = -> Pad016
  Direction = (0,1,0)
  Length = 2
  Length2 = 10
  Profile = -> Pad016 [Face13,Face34,Face50]
  Type = 0
FEATURE [App::Link] Baseplate  label="Baseplate001"
  AssemblyType = Part::Link
  AttachedBy = #LCS_0002
  AttachedTo = Parent Assembly#LCS_Origin
  LinkedObject = -> Part_2
  SolverId = Asm4EE
  expr: Placement = LCS_Origin.Placement * AttachmentOffset * LCS_0002.Placement ^ -1
FEATURE [PartDesign::Pocket] Pocket005
  BaseFeature = -> Pad017
  Direction = (0,0,-1)
  Length = 1
  Length2 = 5
  Profile = -> Pad017 [Face34,Face23,Face25,Face24]
  Type = 0
FEATURE [PartDesign::Pocket] Pocket006
  BaseFeature = -> Pad012
  Direction = (0,0,-1)
  Length = 1
  Length2 = 5
  Profile = -> Pad012 [Face8]
  Type = 0
FEATURE [Sketcher::SketchObject] Sketch020
  FullyConstrained = true
  MapMode = 5
  Placement = pos=(1,0,0) rot=(0.57735,0.57735,0.57735;2.0944rad)
  Support = -> [Pocket006]
  sketch-geometry (1):
    g0: Circle CenterX=0 CenterY=-0.3 CenterZ=0 NormalX=0 NormalY=0 NormalZ=1 AngleXU=0 Radius=0.65
  constraints (3):
    c: PointOnObject(g0,g-2)
    c: Radius(g0) = 0.65
    c: DistanceY(g0,g-1) = 0.3
FEATURE [PartDesign::Pocket] Pocket007
  BaseFeature = -> Pocket006
  Direction = (-1,0,0)
  Length = 5
  Length2 = 5
  Profile = -> Sketch020
  ReferenceAxis = -> Sketch020 [N_Axis]
  Type = 1
FEATURE [PartDesign::Body] Body_2
  Group = -> [Sketch013,Pad011,Sketch014,Pad012,Pocket006,Sketch020,Pocket007]
  Origin = -> Origin008
  Tip = -> Pocket007
FEATURE [PartDesign::CoordinateSystem] LCS_1
  AttacherType = Attacher::AttachEngine3D
  MapMode = 45
  Placement = pos=(0,0,-4) rot=(0,0.707107,0.707107;3.14159rad)
  Support = -> [Pocket007]
FEATURE [App::Part] Part_1  label="spring"
  Group = -> [LCS_0,Body_2,LCS_1]
  Origin = -> Origin007
FEATURE [PartDesign::CoordinateSystem] LCS_2
  AttacherType = Attacher::AttachEngine3D
  MapMode = 45
  Placement = pos=(3.31163,-2.85,-4) rot=(0,0.707107,0.707107;3.14159rad)
  Support = -> [Pocket005]
FEATURE [PartDesign::CoordinateSystem] LCS_3
  AttacherType = Attacher::AttachEngine3D
  MapMode = 45
  Placement = pos=(-2.22398,-5,-4) rot=(0,0.707107,0.707107;3.14159rad)
  Support = -> [Pocket005]
FEATURE [PartDesign::Pad] Pad018
  BaseFeature = -> Pocket005
  Direction = (1,0,0)
  Length = 1
  Length2 = 10
  Profile = -> Pocket005 [Face6]
  Type = 0
FEATURE [PartDesign::Pocket] Pocket008
  BaseFeature = -> Pad018
  Direction = (0,-1,0)
  Length = 0.1
  Length2 = 5
  Profile = -> Pad018 [Face21]
  Type = 0
FEATURE [PartDesign::Pocket] Pocket009
  BaseFeature = -> Pocket008
  Direction = (0,1,0)
  Length = 0.1
  Length2 = 5
  Profile = -> Pocket008 [Face22]
  Type = 0
FEATURE [PartDesign::Pocket] Pocket010
  BaseFeature = -> Pocket009
  Direction = (0,-1,0)
  Length = 0.1
  Length2 = 5
  Profile = -> Pocket009 [Face13]
  Type = 0
FEATURE [PartDesign::Pocket] Pocket011
  BaseFeature = -> Pocket010
  Direction = (0,1,0)
  Length = 0.1
  Length2 = 5
  Profile = -> Pocket010 [Face7]
  Type = 0
FEATURE [PartDesign::Body] Body002
  Group = -> [Sketch015,Pad013,Sketch016,Pad014,Sketch017,Pad015,Sketch018,Pocket003,Fillet001,Sketch019,Pocket004,Pad016,Pad017,Pocket005,Pad018,Pocket008,Pocket009,Pocket010,Pocket011]
  Origin = -> Origin010
  Tip = -> Pocket011
FEATURE [App::Part] Part_2  label="Baseplate"
  Group = -> [LCS_0002,Body002,LCS_2,LCS_3]
  Origin = -> Origin009
FEATURE [App::Link] spring  label="spring001"
  AssemblyType = Part::Link
  AttachedBy = #LCS_1
  AttachedTo = Baseplate#LCS_2
  AttachmentOffset = pos=(-0.3,0,0) rot=(0,0,1;0rad)
  LinkPlacement = pos=(3.61163,-2.85,0) rot=(0,0,1;0rad)
  LinkedObject = -> Part_1
  Placement = pos=(3.61163,-2.85,0) rot=(0,0,1;0rad)
  SolverId = Asm4EE
  expr: Placement = Baseplate.Placement * LCS_2.Placement * AttachmentOffset * LCS_1.Placement ^ -1
FEATURE [App::Link] spring001  label="spring002"
  AssemblyType = Part::Link
  AttachedBy = #LCS_1
  AttachedTo = Baseplate#LCS_3
  AttachmentOffset = pos=(0.3,0,0) rot=(0,1,0;3.14159rad)
  LinkPlacement = pos=(-2.52398,-5,0) rot=(0,0,1;3.14159rad)
  LinkedObject = -> Part_1
  Placement = pos=(-2.52398,-5,0) rot=(0,0,1;3.14159rad)
  SolverId = Asm4EE
  expr: Placement = Baseplate.Placement * LCS_3.Placement * AttachmentOffset * LCS_1.Placement ^ -1
FEATURE [App::Part] Model
  AssemblyType = Part::Link
  Group = -> [LCS_Origin,Constraints,Variables,Configurations,Baseplate,spring,spring001]
  Origin = -> Origin006
  Type = Assembly
FEATURE [PartDesign::CoordinateSystem] LCS_0003
  AttacherType = Attacher::AttachEngine3D
  MapMode = 2
  Support = -> [X_Axis011]
FEATURE [PartDesign::CoordinateSystem] LCS_0004
  AttacherType = Attacher::AttachEngine3D
  MapMode = 2
  Support = -> [X_Axis012]
FEATURE [Mesh::Feature] baseplate_left
FEATURE [Part::Feature] baseplate_left001
  shape: bbox 500 x 500 x 2.3 mm, 632 faces, 0 solids (baked)
FEATURE [Part::Refine] baseplate_left001001
  Source = -> baseplate_left001
FEATURE [Part::Feature] baseplate_left001001_solid  label="baseplate_left001001 (Solid)"
  shape: bbox 500 x 500 x 2.3 mm, 130 faces (baked)
FEATURE [PartDesign::FeatureBase] BaseFeature
  BaseFeature = -> baseplate_left001001_solid
FEATURE [Sketcher::SketchObject] Sketch021
  ExternalGeometry = -> [BaseFeature]
  FullyConstrained = true
  MapMode = 5
  Placement = pos=(0,0,0) rot=(0,1,0;3.14159rad)
  Support = -> [XY_Plane012]
  sketch-geometry (16):
    g0: LineSegment StartX=-211.098 StartY=171.423 StartZ=0 EndX=-187.375 EndY=147.7 EndZ=0
    g1: LineSegment StartX=-211.098 StartY=171.423 StartZ=0 EndX=-200.845 EndY=181.676 EndZ=0
    g2: LineSegment StartX=-200.845 StartY=181.676 StartZ=0 EndX=-190.592 EndY=171.423 EndZ=0
    g3: LineSegment StartX=-190.592 StartY=171.423 StartZ=0 EndX=-200.845 EndY=161.17 EndZ=0
    g4: LineSegment StartX=-200.845 StartY=161.17 StartZ=0 EndX=-211.098 EndY=171.423 EndZ=0
    g5: LineSegment StartX=-187.375 StartY=147.7 StartZ=0 EndX=-177.122 EndY=157.953 EndZ=0
    g6: LineSegment StartX=-177.122 StartY=157.953 StartZ=0 EndX=-187.375 EndY=168.206 EndZ=0
    g7: LineSegment StartX=-187.375 StartY=168.206 StartZ=0 EndX=-197.628 EndY=157.953 EndZ=0
    g8: LineSegment StartX=-197.628 StartY=157.953 StartZ=0 EndX=-187.375 EndY=147.7 EndZ=0
    g9: LineSegment StartX=-180.64 StartY=167.906 StartZ=0 EndX=-170.387 EndY=178.159 EndZ=0
    g10: LineSegment StartX=-170.387 StartY=178.159 StartZ=0 EndX=-180.64 EndY=188.412 EndZ=0
    g11: LineSegment StartX=-180.64 StartY=188.412 StartZ=0 EndX=-190.893 EndY=178.159 EndZ=0
    g12: LineSegment StartX=-190.893 StartY=178.159 StartZ=0 EndX=-180.64 EndY=167.906 EndZ=0
    g13: LineSegment StartX=-190.592 StartY=171.423 StartZ=0 EndX=-187.375 EndY=174.641 EndZ=0
    g14: LineSegment StartX=-200.845 StartY=181.676 StartZ=0 EndX=-190.893 EndY=178.159 EndZ=0
    g15: LineSegment StartX=-180.64 StartY=167.906 StartZ=0 EndX=-177.122 EndY=157.953 EndZ=0
  constraints (45):
    c: Coincident(g1,g2)
    c: Coincident(g2,g3)
    c: Coincident(g3,g4)
    c: Coincident(g4,g1)
    c: PointOnObject(g3,g0)
    c: Equal(g4,g3)
    c: Equal(g3,g1)
    c: Equal(g1,g2)
    c: Perpendicular(g4,g1)
    c: Distance(g1) = 14.5
    c: Coincident(g0,g1)
    c: Coincident(g0,g5)
    c: Coincident(g5,g6)
    c: Coincident(g6,g7)
    c: PointOnObject(g7,g0)
    c: Coincident(g7,g8)
    c: Coincident(g8,g5)
    c: Equal(g7,g8)
    c: Equal(g8,g6)
    c: Equal(g6,g5)
    c: Equal(g5,g4)
    c: Perpendicular(g8,g7)
    c: Distance(g1,g7) = 19.05
    c: Coincident(g9,g10)
    c: Coincident(g10,g11)
    c: Coincident(g11,g12)
    c: Coincident(g12,g9)
    c: Equal(g11,g12)
    c: Equal(g12,g10)
    c: Equal(g10,g9)
    c: Perpendicular(g12,g11)
    c: Parallel(g2,g12)
    c: Coincident(g13,g2)
    c: PointOnObject(g13,g12)
    c: Perpendicular(g12,g13)
    c: Distance(g13,g3) = 19.05
    c: Coincident(g14,g1)
    c: Coincident(g14,g11)
    c: Coincident(g15,g9)
    c: Coincident(g15,g5)
    c: Equal(g15,g14)
    c: Equal(g6,g10)
    c: Angle(g8,g-1) = 0.785398
    c: DistanceX(g-3,g5) = 20
    c: DistanceY(g-3,g5) = 7
FEATURE [PartDesign::Pocket] Pocket012
  BaseFeature = -> BaseFeature
  Direction = (0,0,1)
  Length = 5
  Length2 = 5
  Profile = -> Sketch021
  ReferenceAxis = -> Sketch021 [N_Axis]
  Type = 0
FEATURE [Sketcher::SketchObject] Sketch022
  ExternalGeometry = -> [Pocket012]
  FullyConstrained = false
  MapMode = 5
  Placement = pos=(0,0,2.3) rot=(0,0,1;0rad)
  Support = -> [Pocket012]
  sketch-geometry (22):
    g0: LineSegment StartX=160.64 StartY=198.412 StartZ=0 EndX=200.64 EndY=198.412 EndZ=0
    g1: LineSegment StartX=49.525 StartY=40 StartZ=0 EndX=263.025 EndY=40 EndZ=0
    g2: LineSegment StartX=227.375 StartY=106.5 StartZ=0 EndX=230.175 EndY=106.5 EndZ=0
    g3: LineSegment StartX=230.175 StartY=106.5 StartZ=0 EndX=230.175 EndY=50 EndZ=0
    g4: LineSegment StartX=230.175 StartY=50 StartZ=0 EndX=227.375 EndY=50 EndZ=0
    g5: LineSegment StartX=227.375 StartY=50 StartZ=0 EndX=227.375 EndY=106.5 EndZ=0
    g6: LineSegment StartX=253.025 StartY=106.5 StartZ=0 EndX=250.225 EndY=106.5 EndZ=0
    g7: LineSegment StartX=250.225 StartY=106.5 StartZ=0 EndX=250.225 EndY=50 EndZ=0
    g8: LineSegment StartX=250.225 StartY=50 StartZ=0 EndX=253.025 EndY=50 EndZ=0
    g9: LineSegment StartX=253.025 StartY=50 StartZ=0 EndX=253.025 EndY=106.5 EndZ=0
    g10: LineSegment StartX=227.375 StartY=106.5 StartZ=0 EndX=228.775 EndY=106.5 EndZ=0
    g11: LineSegment StartX=228.775 StartY=106.5 StartZ=0 EndX=230.175 EndY=106.5 EndZ=0
    g12: LineSegment StartX=253.025 StartY=106.5 StartZ=0 EndX=251.625 EndY=106.5 EndZ=0
    g13: LineSegment StartX=251.625 StartY=106.5 StartZ=0 EndX=250.225 EndY=106.5 EndZ=0
    g14: LineSegment StartX=200.64 StartY=198.412 StartZ=0 EndX=263.025 EndY=163.412 EndZ=0
    g15: LineSegment StartX=263.025 StartY=163.412 StartZ=0 EndX=263.025 EndY=40 EndZ=0
    g16: LineSegment StartX=49.525 StartY=40 StartZ=0 EndX=49.525 EndY=163.412 EndZ=0
    g17: LineSegment StartX=49.525 StartY=163.412 StartZ=0 EndX=160.64 EndY=198.412 EndZ=0
    g18: LineSegment StartX=0 StartY=0 StartZ=0 EndX=511.801 EndY=0 EndZ=0
    g19: LineSegment StartX=511.801 StartY=0 StartZ=0 EndX=511.801 EndY=507.959 EndZ=0
    g20: LineSegment StartX=511.801 StartY=507.959 StartZ=0 EndX=0 EndY=507.959 EndZ=0
    g21: LineSegment StartX=0 StartY=507.959 StartZ=0 EndX=0 EndY=0 EndZ=0
  constraints (61):
    c: Coincident(g0,g14)
    c: Coincident(g17,g0)
    c: Coincident(g1,g15)
    c: Coincident(g2,g3)
    c: Coincident(g3,g4)
    c: Coincident(g4,g5)
    c: Coincident(g5,g2)
    c: Horizontal(g2)
    c: Horizontal(g4)
    c: Vertical(g3)
    c: Vertical(g5)
    c: Coincident(g6,g7)
    c: Coincident(g7,g8)
    c: Coincident(g8,g9)
    c: Coincident(g9,g6)
    c: Horizontal(g6)
    c: Horizontal(g8)
    c: Vertical(g7)
    c: Vertical(g9)
    c: Coincident(g10,g2)
    c: Coincident(g11,g10)
    c: Coincident(g11,g2)
    c: Equal(g11,g10)
    c: PointOnObject(g10,g2)
    c: Coincident(g6,g12)
    c: Coincident(g12,g13)
    c: Coincident(g13,g6)
    c: Equal(g13,g12)
    c: PointOnObject(g12,g6)
    c: DistanceX(g10,g12) = 22.85
    c: Equal(g2,g6)
    c: DistanceX(g4,g4) = 2.8
    c: DistanceY(g5,g5) = 56.5
    c: PointOnObject(g6,g2)
    c: PointOnObject(g8,g4)
    c: Horizontal(g1)
    c: DistanceX(g-3,g2) = 20
    c: DistanceY(g4,g-4) = 0
    c: DistanceY(g15,g-4) = 10
    c: DistanceX(g16,g-6) = 10
    c: DistanceX(g8,g15) = 10
    c: Coincident(g14,g15)
    c: Vertical(g15)
    c: Horizontal(g0)
    c: DistanceY(g-5,g0) = 10
    c: Coincident(g16,g17)
    c: Vertical(g16)
    c: DistanceY(g16,g-5) = 25
    c: DistanceY(g14,g-5) = 25
    c: DistanceX(g0,g-5) = 20
    c: DistanceX(g-5,g0) = 20
    c: Coincident(g1,g16)
    c: Coincident(g18,g19)
    c: Coincident(g19,g20)
    c: Coincident(g20,g21)
    c: Coincident(g21,g18)
    c: Horizontal(g18)
    c: Horizontal(g20)
    c: Vertical(g19)
    c: Vertical(g21)
    c: Coincident(g18,g-1)
FEATURE [PartDesign::Pocket] Pocket013
  BaseFeature = -> Pocket012
  Direction = (0,0,-1)
  Length = 5
  Length2 = 5
  Profile = -> Sketch022
  ReferenceAxis = -> Sketch022 [N_Axis]
  Type = 0
FEATURE [PartDesign::CoordinateSystem] LCS_0005
  AttacherType = Attacher::AttachEngine3D
  MapMode = 2
  Support = -> [X_Axis]
FEATURE [Mesh::Feature] baseplate_right
FEATURE [Part::Feature] baseplate_right001
  shape: bbox 500 x 500 x 2.3 mm, 652 faces, 0 solids (baked)
FEATURE [Part::Refine] baseplate_right001001
  Source = -> baseplate_right001
FEATURE [Part::Feature] baseplate_right001001_solid  label="baseplate_right001001 (Solid)"
  shape: bbox 500 x 500 x 2.3 mm, 134 faces (baked)
FEATURE [PartDesign::FeatureBase] BaseFeature001
  BaseFeature = -> baseplate_right001001_solid
FEATURE [Sketcher::SketchObject] Sketch024
  ExternalGeometry = -> [BaseFeature001]
  FullyConstrained = true
  MapMode = 5
  Placement = pos=(0,0,0) rot=(1,0,0;3.14159rad)
  Support = -> [BaseFeature001]
  expr: Constraints[40] = 1.25 * 19.05
  sketch-geometry (16):
    g0: LineSegment StartX=42.6282 StartY=-166.401 StartZ=0 EndX=64.1937 EndY=-140.7 EndZ=0
    g1: LineSegment StartX=42.6282 StartY=-166.401 StartZ=0 EndX=31.5206 EndY=-157.08 EndZ=0
    g2: LineSegment StartX=31.5206 StartY=-157.08 StartZ=0 EndX=40.841 EndY=-145.973 EndZ=0
    g3: LineSegment StartX=40.841 StartY=-145.973 StartZ=0 EndX=51.9486 EndY=-155.293 EndZ=0
    g4: LineSegment StartX=51.9486 StartY=-155.293 StartZ=0 EndX=42.6282 EndY=-166.401 EndZ=0
    g5: LineSegment StartX=54.8733 StartY=-151.808 StartZ=0 EndX=43.7657 EndY=-142.487 EndZ=0
    g6: LineSegment StartX=43.7657 StartY=-142.487 StartZ=0 EndX=53.0861 EndY=-131.38 EndZ=0
    g7: LineSegment StartX=53.0861 StartY=-131.38 StartZ=0 EndX=64.1937 EndY=-140.7 EndZ=0
    g8: LineSegment StartX=64.1937 StartY=-140.7 StartZ=0 EndX=54.8733 EndY=-151.808 EndZ=0
    g9: LineSegment StartX=42.6282 StartY=-166.401 StartZ=0 EndX=53.411 EndY=-153.55 EndZ=0
    g10: LineSegment StartX=53.411 StartY=-153.55 StartZ=0 EndX=64.1937 EndY=-140.7 EndZ=0
    g11: LineSegment StartX=53.411 StartY=-153.55 StartZ=0 EndX=71.6524 EndY=-168.857 EndZ=0
    g12: LineSegment StartX=65.205 StartY=-153.983 StartZ=0 EndX=76.3126 EndY=-163.303 EndZ=0
    g13: LineSegment StartX=76.3126 StartY=-163.303 StartZ=0 EndX=66.9922 EndY=-174.411 EndZ=0
    g14: LineSegment StartX=66.9922 StartY=-174.411 StartZ=0 EndX=55.8846 EndY=-165.09 EndZ=0
    g15: LineSegment StartX=55.8846 StartY=-165.09 StartZ=0 EndX=65.205 EndY=-153.983 EndZ=0
  constraints (44):
    c: Coincident(g0,g1)
    c: Coincident(g1,g2)
    c: Coincident(g2,g3)
    c: PointOnObject(g3,g0)
    c: Coincident(g3,g4)
    c: Coincident(g4,g1)
    c: PointOnObject(g5,g0)
    c: Coincident(g5,g6)
    c: Coincident(g6,g7)
    c: Coincident(g7,g0)
    c: Coincident(g7,g8)
    c: Coincident(g8,g5)
    c: Equal(g1,g2)
    c: Equal(g2,g3)
    c: Equal(g3,g4)
    c: Equal(g4,g5)
    c: Equal(g5,g6)
    c: Equal(g6,g7)
    c: Equal(g7,g8)
    c: Perpendicular(g8,g5)
    c: Perpendicular(g4,g1)
    c: Distance(g1,g5) = 19.05
    c: Distance(g2) = 14.5
    c: Coincident(g9,g1)
    c: Coincident(g10,g9)
    c: Coincident(g10,g7)
    c: Equal(g9,g10)
    c: PointOnObject(g9,g0)
    c: Coincident(g11,g9)
    c: Perpendicular(g0,g11)
    c: Coincident(g12,g13)
    c: Coincident(g13,g14)
    c: Coincident(g14,g15)
    c: Coincident(g15,g12)
    c: Symmetric(g12,g14,g11)
    c: Symmetric(g12,g13,g11)
    c: Equal(g12,g15)
    c: Equal(g14,g13)
    c: Equal(g13,g8)
    c: PointOnObject(g11,g13)
    c: Distance(g11,g9) = 23.8125
    c: Angle(g7,g-3) = 0.698132
    c: DistanceX(g7,g-3) = 12
    c: PointOnObject(g7,g-3)
FEATURE [PartDesign::Pocket] Pocket014
  BaseFeature = -> BaseFeature001
  Direction = (0,0,1)
  Length = 5
  Length2 = 5
  Profile = -> Sketch024
  ReferenceAxis = -> Sketch024 [N_Axis]
  Type = 0
FEATURE [Sketcher::SketchObject] Sketch025
  ExternalGeometry = -> [Pocket014]
  FullyConstrained = true
  MapMode = 5
  Placement = pos=(0,0,0) rot=(1,0,0;3.14159rad)
  Support = -> [Pocket014]
  sketch-geometry (24):
    g0: LineSegment StartX=0.875002 StartY=-43 StartZ=0 EndX=214.375 EndY=-43 EndZ=0
    g1: LineSegment StartX=214.375 StartY=-43 StartZ=0 EndX=214.375 EndY=-143.007 EndZ=0
    g2: LineSegment StartX=214.375 StartY=-143.007 StartZ=0 EndX=66.9922 EndY=-181.411 EndZ=0
    g3: LineSegment StartX=66.9922 StartY=-181.411 StartZ=0 EndX=0.875002 EndY=-160.593 EndZ=0
    g4: LineSegment StartX=0.875002 StartY=-160.593 StartZ=0 EndX=0.875002 EndY=-43 EndZ=0
    g5: LineSegment StartX=42.6282 StartY=-166.401 StartZ=0 EndX=40.526 EndY=-173.078 EndZ=0
    g6: LineSegment StartX=66.9922 StartY=-181.411 StartZ=0 EndX=66.9922 EndY=-174.411 EndZ=0
    g7: LineSegment StartX=195.469 StartY=-140.7 StartZ=0 EndX=197.234 EndY=-147.474 EndZ=0
    g8: LineSegment StartX=8.875 StartY=-50 StartZ=0 EndX=11.675 EndY=-50 EndZ=0
    g9: LineSegment StartX=11.675 StartY=-50 StartZ=0 EndX=11.675 EndY=-106.5 EndZ=0
    g10: LineSegment StartX=11.675 StartY=-106.5 StartZ=0 EndX=8.875 EndY=-106.5 EndZ=0
    g11: LineSegment StartX=8.875 StartY=-106.5 StartZ=0 EndX=8.875 EndY=-50 EndZ=0
    g12: LineSegment StartX=31.725 StartY=-50 StartZ=0 EndX=34.525 EndY=-50 EndZ=0
    g13: LineSegment StartX=34.525 StartY=-50 StartZ=0 EndX=34.525 EndY=-106.5 EndZ=0
    g14: LineSegment StartX=34.525 StartY=-106.5 StartZ=0 EndX=31.725 EndY=-106.5 EndZ=0
    g15: LineSegment StartX=31.725 StartY=-106.5 StartZ=0 EndX=31.725 EndY=-50 EndZ=0
    g16: LineSegment StartX=8.875 StartY=-50 StartZ=0 EndX=10.275 EndY=-50 EndZ=0
    g17: LineSegment StartX=10.275 StartY=-50 StartZ=0 EndX=11.675 EndY=-50 EndZ=0
    g18: LineSegment StartX=31.725 StartY=-50 StartZ=0 EndX=33.125 EndY=-50 EndZ=0
    g19: LineSegment StartX=33.125 StartY=-50 StartZ=0 EndX=34.525 EndY=-50 EndZ=0
    g20: LineSegment StartX=0 StartY=0 StartZ=0 EndX=798.95 EndY=0 EndZ=0
    g21: LineSegment StartX=798.95 StartY=0 StartZ=0 EndX=798.95 EndY=-762.419 EndZ=0
    g22: LineSegment StartX=798.95 StartY=-762.419 StartZ=0 EndX=0 EndY=-762.419 EndZ=0
    g23: LineSegment StartX=0 StartY=-762.419 StartZ=0 EndX=0 EndY=0 EndZ=0
  constraints (68):
    c: Horizontal(g0)
    c: Coincident(g0,g1)
    c: Vertical(g1)
    c: Coincident(g1,g2)
    c: Coincident(g2,g3)
    c: Coincident(g3,g4)
    c: Coincident(g4,g0)
    c: Vertical(g4)
    c: DistanceX(g-3,g1) = 7
    c: Coincident(g5,g-4)
    c: PointOnObject(g5,g3)
    c: Perpendicular(g3,g5)
    c: Distance(g5) = 7
    c: Coincident(g6,g2)
    c: Coincident(g6,g-5)
    c: Vertical(g6)
    c: DistanceY(g6,g6) = 7
    c: Coincident(g7,g-6)
    c: PointOnObject(g7,g2)
    c: Perpendicular(g2,g7)
    c: Distance(g7) = 7
    c: DistanceY(g-7,g0) = 7
    c: Coincident(g8,g9)
    c: Coincident(g9,g10)
    c: Coincident(g10,g11)
    c: Coincident(g11,g8)
    c: Horizontal(g8)
    c: Horizontal(g10)
    c: Vertical(g9)
    c: Vertical(g11)
    c: Coincident(g12,g13)
    c: Coincident(g13,g14)
    c: Coincident(g14,g15)
    c: Coincident(g15,g12)
    c: Horizontal(g12)
    c: Horizontal(g14)
    c: Vertical(g13)
    c: Vertical(g15)
    c: Coincident(g16,g8)
    c: Coincident(g17,g16)
    c: Coincident(g17,g8)
    c: Equal(g17,g16)
    c: Horizontal(g16)
    c: Coincident(g12,g18)
    c: Coincident(g18,g19)
    c: Coincident(g19,g12)
    c: Equal(g19,g18)
    c: Horizontal(g19)
    c: PointOnObject(g8,g12)
    c: Equal(g11,g15)
    c: Equal(g10,g14)
    c: DistanceX(g16,g18) = 22.85
    c: DistanceY(g11,g11) = 56.5
    c: DistanceX(g10,g10) = 2.8
    c: DistanceY(g8,g0) = 7
    c: DistanceX(g0,g8) = 8
    c: Coincident(g20,g21)
    c: Coincident(g21,g22)
    c: Coincident(g22,g23)
    c: Coincident(g23,g20)
    c: Horizontal(g20)
    c: Horizontal(g22)
    c: Vertical(g21)
    c: Vertical(g23)
    c: Coincident(g20,g-1)
    c: DistanceX(g21) = 798.95
    c: DistanceY(g21) = -762.419
    c: DistanceX(g12,g-8) = 25
FEATURE [PartDesign::Pocket] Pocket015
  BaseFeature = -> Pocket014
  Direction = (0,0,1)
  Length = 5
  Length2 = 5
  Profile = -> Sketch025
  ReferenceAxis = -> Sketch025 [N_Axis]
  Type = 0
FEATURE [Sketcher::SketchObject] Sketch026
  ExternalGeometry = -> [Pocket015]
  FullyConstrained = true
  MapMode = 5
  Placement = pos=(0,0,2.3) rot=(0,0,1;0rad)
  Support = -> [Pocket015]
  sketch-geometry (10):
    g0: LineSegment StartX=0.875002 StartY=160.593 StartZ=0 EndX=66.9922 EndY=181.411 EndZ=0
    g1: LineSegment StartX=66.9922 StartY=181.411 StartZ=0 EndX=214.375 EndY=143.007 EndZ=0
    g2: LineSegment StartX=214.375 StartY=143.007 StartZ=0 EndX=214.375 EndY=43 EndZ=0
    g3: LineSegment StartX=214.375 StartY=43 StartZ=0 EndX=0.875002 EndY=43 EndZ=0
    g4: LineSegment StartX=0.875002 StartY=43 StartZ=0 EndX=0.875002 EndY=160.593 EndZ=0
    g5: LineSegment StartX=212.375 StartY=141.462 StartZ=0 EndX=212.375 EndY=45 EndZ=0
    g6: LineSegment StartX=212.375 StartY=45 StartZ=0 EndX=2.875 EndY=45 EndZ=0
    g7: LineSegment StartX=2.875 StartY=45 StartZ=0 EndX=2.875 EndY=159.126 EndZ=0
    g8: LineSegment StartX=2.875 StartY=159.126 StartZ=0 EndX=67.0444 EndY=179.33 EndZ=0
    g9: LineSegment StartX=67.0444 StartY=179.33 StartZ=0 EndX=212.375 EndY=141.462 EndZ=0
  constraints (21):
    c: Coincident(g-7,g0)
    c: Coincident(g0,g-4)
    c: Coincident(g0,g1)
    c: Coincident(g1,g-5)
    c: Coincident(g1,g2)
    c: Coincident(g2,g-6)
    c: Coincident(g2,g3)
    c: Coincident(g3,g-7)
    c: Coincident(g3,g4)
    c: Coincident(g4,g0)
    c: Coincident(g5,g6)
    c: Coincident(g5,g9)
    c: Coincident(g6,g7)
    c: Coincident(g7,g8)
    c: Coincident(g8,g9)
    c: Block(g9)
    c: Block(g5)
    c: Parallel(g0,g8)
    c: DistanceX(g3,g6) = 2
    c: Vertical(g7)
    c: Horizontal(g6)
FEATURE [PartDesign::Pad] Pad020
  BaseFeature = -> Pocket015
  Direction = (0,0,1)
  Length = 15
  Length2 = 10
  Profile = -> Sketch026
  ReferenceAxis = -> Sketch026 [N_Axis]
  Type = 0
FEATURE [Sketcher::SketchObject] Sketch027
  ExternalGeometry = -> [Pad020]
  FullyConstrained = true
  MapMode = 5
  Placement = pos=(0,0,2.3) rot=(0,0,1;0rad)
  Support = -> [Pad020]
  sketch-geometry (10):
    g0: LineSegment StartX=88.1 StartY=64.5 StartZ=0 EndX=88.1 EndY=66.775 EndZ=0
    g1: LineSegment StartX=88.1 StartY=66.775 StartZ=0 EndX=88.1 EndY=69.05 EndZ=0
    g2: LineSegment StartX=88.1 StartY=66.775 StartZ=0 EndX=212.375 EndY=66.775 EndZ=0
    g3: LineSegment StartX=56.525 StartY=66 StartZ=0 EndX=56.525 EndY=67.55 EndZ=0
    g4: LineSegment StartX=56.525 StartY=67.55 StartZ=0 EndX=212.375 EndY=67.55 EndZ=0
    g5: LineSegment StartX=212.375 StartY=67.55 StartZ=0 EndX=212.375 EndY=66 EndZ=0
    g6: LineSegment StartX=212.375 StartY=66 StartZ=0 EndX=56.525 EndY=66 EndZ=0
    g7: GeomPoint X=134.45 Y=66.775 Z=0
    g8: LineSegment StartX=97.625 StartY=83.55 StartZ=0 EndX=97.625 EndY=85.825 EndZ=0
    g9: LineSegment StartX=97.625 StartY=85.825 StartZ=0 EndX=97.625 EndY=88.1 EndZ=0
  constraints (29):
    c: Coincident(g-4,g0)
    c: Vertical(g0)
    c: Coincident(g0,g1)
    c: Vertical(g1)
    c: Equal(g1,g0)
    c: Coincident(g2,g0)
    c: PointOnObject(g2,g-3)
    c: Horizontal(g2)
    c: Coincident(g3,g4)
    c: Coincident(g4,g5)
    c: Coincident(g5,g6)
    c: Coincident(g6,g3)
    c: Vertical(g3)
    c: Vertical(g5)
    c: Horizontal(g4)
    c: Horizontal(g6)
    c: Symmetric(g5,g3,g7)
    c: PointOnObject(g7,g2)
    c: PointOnObject(g5,g-3)
    c: PointOnObject(g1,g-5)
    c: DistanceY(g0,g3) = 1.5
    c: DistanceX(g-6,g3) = 22
    c: Coincident(g8,g-7)
    c: Vertical(g8)
    c: Coincident(g9,g8)
    c: PointOnObject(g9,g-8)
    c: Vertical(g9)
    c: Equal(g9,g8)
    c: DistanceY(g0,g8) = 19.05  'wall_row_distance'
FEATURE [PartDesign::Pad] Pad021
  BaseFeature = -> Pad020
  Direction = (0,0,1)
  Length = 20
  Length2 = 10
  Profile = -> Sketch027
  ReferenceAxis = -> Sketch027 [N_Axis]
  Type = 3
  UpToFace = -> Pad020 [Face161]
FEATURE [PartDesign::LinearPattern] LinearPattern
  BaseFeature = -> Pad021
  Direction = -> Sketch027 [V_Axis]
  Length = 57.15
  Mode = 0
  Occurrences = 4
  Offset = 19.05
  Originals = -> [Pad021]
  expr: Length = Sketch027.Constraints.wall_row_distance * (Occurrences - 1)
FEATURE [PartDesign::Pad] Pad022
  BaseFeature = -> LinearPattern
  Direction = (-1,0,0)
  Length = 10
  Length2 = 10
  Profile = -> LinearPattern [Face164]
  Type = 2
FEATURE [PartDesign::Pad] Pad023
  BaseFeature = -> Pad022
  Direction = (-1,0,0)
  Length = 2
  Length2 = 10
  Profile = -> Pad022 [Face170]
  Type = 0
FEATURE [PartDesign::Pad] Pad024
  BaseFeature = -> Pad023
  Direction = (0,-1,0)
  Length = 10
  Length2 = 10
  Profile = -> Pad023 [Face171]
  Type = 2
FEATURE [PartDesign::Pad] Pad025
  BaseFeature = -> Pad024
  Direction = (0,1,0)
  Length = 10
  Length2 = 10
  Profile = -> Pad024 [Face179]
  Type = 2
FEATURE [PartDesign::Pocket] Pocket016
  BaseFeature = -> Pad025
  Direction = (0,0,-1)
  Length = 8
  Length2 = 5
  Profile = -> Pad025 [Face201,Face202,Face199]
  Type = 0
FEATURE [PartDesign::Pocket] Pocket017
  BaseFeature = -> Pocket016
  Direction = (0,0,-1)
  Length = 8
  Length2 = 5
  Profile = -> Pocket016 [Face200]
  Type = 0
FEATURE [PartDesign::Pad] Pad026
  BaseFeature = -> Pocket013
  Direction = (1,0,0)
  Length = 10
  Length2 = 10
  Profile = -> Pocket013 [Face117]
  Type = 2
FEATURE [PartDesign::Body] Body_3  label="plate_left"
  BaseFeature = -> baseplate_left001001_solid
  Group = -> [BaseFeature,LCS_0004,Sketch021,Pocket012,Sketch022,Pocket013,Pad026]
  Origin = -> Origin012
  Tip = -> Pocket013
FEATURE [PartDesign::Pocket] Pocket018
  BaseFeature = -> Pocket017
  Direction = (0,0,1)
  Length = 0.9
  Length2 = 5
  Profile = -> Pocket017 [Face1]
  Type = 0
FEATURE [Sketcher::SketchObject] Sketch028
  FullyConstrained = false
  MapMode = 5
  Placement = pos=(0,0,0.9) rot=(1,0,0;3.14159rad)
  Support = -> [Pocket018]
  sketch-geometry (8):
    g0: LineSegment StartX=186.641 StartY=-48.1554 StartZ=0 EndX=186.641 EndY=-65.87 EndZ=0
    g1: LineSegment StartX=186.641 StartY=-65.87 StartZ=0 EndX=203.656 EndY=-65.87 EndZ=0
    g2: LineSegment StartX=203.656 StartY=-65.87 StartZ=0 EndX=203.656 EndY=-48.1554 EndZ=0
    g3: LineSegment StartX=203.656 StartY=-48.1554 StartZ=0 EndX=186.641 EndY=-48.1554 EndZ=0
    g4: LineSegment StartX=-16.894 StartY=-28.9206 StartZ=0 EndX=-16.894 EndY=-187.952 EndZ=0
    g5: LineSegment StartX=-16.894 StartY=-187.952 StartZ=0 EndX=239.258 EndY=-187.952 EndZ=0
    g6: LineSegment StartX=239.258 StartY=-187.952 StartZ=0 EndX=239.258 EndY=-28.9206 EndZ=0
    g7: LineSegment StartX=239.258 StartY=-28.9206 StartZ=0 EndX=-16.894 EndY=-28.9206 EndZ=0
  constraints (16):
    c: Coincident(g0,g1)
    c: Coincident(g1,g2)
    c: Coincident(g2,g3)
    c: Coincident(g3,g0)
    c: Vertical(g0)
    c: Vertical(g2)
    c: Horizontal(g1)
    c: Horizontal(g3)
    c: Coincident(g4,g5)
    c: Coincident(g5,g6)
    c: Coincident(g6,g7)
    c: Coincident(g7,g4)
    c: Vertical(g4)
    c: Vertical(g6)
    c: Horizontal(g5)
    c: Horizontal(g7)
FEATURE [PartDesign::Pocket] Pocket019
  BaseFeature = -> Pocket018
  Direction = (0,0,1)
  Length = 5
  Length2 = 5
  Profile = -> Sketch028
  ReferenceAxis = -> Sketch028 [N_Axis]
  Type = 1
FEATURE [Spreadsheet::Sheet] Spreadsheet
  cells = A1(horizontal_pad)=0.4; B1='switch_hole_size; C1='d_key; D1='h_plate; E1='h_wall_out; F1='d_wall_out; G1='h_wall_in; B2(switch_hole_size)=14.1; C2(d_key)=19.05; D2(h_plate)=1.3; E2(h_wall_out)=15; F2(d_wall_out)=2; G2(h_wall_in)=8
FEATURE [PartDesign::Pad] Pad027
  BaseFeature = -> Pocket019
  Direction = (-1,0,0)
  Length = 0.4
  Length2 = 10
  Profile = -> Pocket019 [Face8]
  Type = 0
  expr: Length = Spreadsheet.horizontal_pad
FEATURE [PartDesign::Pad] Pad028
  BaseFeature = -> Pad027
  Direction = (0,-1,0)
  Length = 0.4
  Length2 = 10
  Profile = -> Pad027 [Face6]
  Type = 0
  expr: Length = Spreadsheet.horizontal_pad
FEATURE [PartDesign::Body] plate_right
  BaseFeature = -> baseplate_right001001_solid
  Group = -> [BaseFeature001,LCS_0005,Sketch024,Pocket014,Sketch025,Pocket015,Sketch026,Pad020,Sketch027,Pad021,LinearPattern,Pad022,Pad023,Pad024,Pad025,Pocket016,Pocket017,Pocket018,Sketch028,Pocket019,Pad027,Pad028]
  Origin = -> Origin
  Tip = -> Pocket018
FEATURE [Part::Feature] baseplate_right_v004_solid001  label="oldbaseplate_right_v004 (Solid)"
  shape: bbox 500 x 500 x 1.5 mm, 134 faces (baked)
FEATURE [Sketcher::SketchObject] Sketch032
  AttachmentOffset = pos=(0,0,1.3) rot=(0,0,1;0rad)
  FullyConstrained = true
  MapMode = 5
  Placement = pos=(0,0,1.3) rot=(0,0,1;0rad)
  Support = -> [XY_Plane013]
  expr: .AttachmentOffset.Base.z = Spreadsheet.h_plate
  sketch-geometry (6):
    g0: LineSegment StartX=194.05 StartY=191.575 StartZ=0 EndX=333.212 EndY=191.575 EndZ=0
    g1: LineSegment StartX=333.212 StartY=190.8 StartZ=0 EndX=333.212 EndY=192.35 EndZ=0
    g2: LineSegment StartX=333.212 StartY=192.35 StartZ=0 EndX=178.212 EndY=192.35 EndZ=0
    g3: LineSegment StartX=178.212 StartY=192.35 StartZ=0 EndX=178.212 EndY=190.8 EndZ=0
    g4: LineSegment StartX=178.212 StartY=190.8 StartZ=0 EndX=333.212 EndY=190.8 EndZ=0
    g5: GeomPoint X=255.712 Y=191.575 Z=0
  constraints (14):
    c: Coincident(g1,g2)
    c: Coincident(g2,g3)
    c: Coincident(g3,g4)
    c: Coincident(g4,g1)
    c: Vertical(g1)
    c: Vertical(g3)
    c: Horizontal(g2)
    c: Horizontal(g4)
    c: Symmetric(g3,g1,g5)
    c: PointOnObject(g5,g0)
    c: Block(g0)
    c: DistanceY(g3,g3) = 1.55
    c: PointOnObject(g0,g1)
    c: DistanceX(g4,g4) = 155
FEATURE [Mesh::Feature] baseplate_right_v2
FEATURE [Part::Feature] baseplate_right_v003
  shape: bbox 500 x 500 x 1.3 mm, 652 faces, 0 solids (baked)
FEATURE [Part::Refine] baseplate_right_v004
  Source = -> baseplate_right_v003
FEATURE [Part::Feature] baseplate_right_v004_solid  label="baseplate_right_v004 (Solid)"
  shape: bbox 500 x 500 x 1.3 mm, 134 faces (baked)
FEATURE [PartDesign::FeatureBase] BaseFeature002
  BaseFeature = -> baseplate_right_v004_solid
FEATURE [Sketcher::SketchObject] Sketch029
  AttachmentOffset = pos=(0,0,10) rot=(0,0,1;0rad)
  ExternalGeometry = -> [BaseFeature002]
  FullyConstrained = true
  MapMode = 5
  Placement = pos=(0,0,10) rot=(0,0,1;0rad)
  Support = -> [XY_Plane013]
  expr: Constraints[24] = Spreadsheet.d_key
  expr: Constraints[9] = Spreadsheet.switch_hole_size
  sketch-geometry (19):
    g0: LineSegment StartX=155.753 StartY=278.77 StartZ=0 EndX=145.783 EndY=268.8 EndZ=0
    g1: LineSegment StartX=145.783 StartY=268.8 StartZ=0 EndX=155.753 EndY=258.83 EndZ=0
    g2: LineSegment StartX=155.753 StartY=258.83 StartZ=0 EndX=165.723 EndY=268.8 EndZ=0
    g3: LineSegment StartX=165.723 StartY=268.8 StartZ=0 EndX=155.753 EndY=278.77 EndZ=0
    g4: GeomPoint X=155.753 Y=268.8 Z=0
    g5: LineSegment StartX=169.224 StartY=265.3 StartZ=0 EndX=159.253 EndY=255.33 EndZ=0
    g6: LineSegment StartX=159.253 StartY=255.33 StartZ=0 EndX=169.224 EndY=245.359 EndZ=0
    g7: LineSegment StartX=169.224 StartY=245.359 StartZ=0 EndX=179.194 EndY=255.33 EndZ=0
    g8: LineSegment StartX=179.194 StartY=255.33 StartZ=0 EndX=169.224 EndY=265.3 EndZ=0
    g9: GeomPoint X=169.224 Y=255.33 Z=0
    g10: LineSegment StartX=155.753 StartY=268.8 StartZ=0 EndX=169.224 EndY=255.33 EndZ=0
    g11: LineSegment StartX=180.166 StartY=289.713 StartZ=0 EndX=170.196 EndY=279.742 EndZ=0
    g12: LineSegment StartX=170.196 StartY=279.742 StartZ=0 EndX=180.166 EndY=269.772 EndZ=0
    g13: LineSegment StartX=180.166 StartY=269.772 StartZ=0 EndX=190.136 EndY=279.742 EndZ=0
    g14: LineSegment StartX=190.136 StartY=279.742 StartZ=0 EndX=180.166 EndY=289.713 EndZ=0
    g15: GeomPoint X=180.166 Y=279.742 Z=0
    g16: LineSegment StartX=162.488 StartY=262.065 StartZ=0 EndX=180.166 EndY=279.742 EndZ=0
    g17: LineSegment StartX=179.194 StartY=255.33 StartZ=0 EndX=180.166 EndY=269.772 EndZ=0
    g18: LineSegment StartX=170.196 StartY=279.742 StartZ=0 EndX=155.753 EndY=278.77 EndZ=0
  constraints (49):
    c: Coincident(g0,g1)
    c: Coincident(g1,g2)
    c: Coincident(g2,g3)
    c: Coincident(g3,g0)
    c: Symmetric(g2,g0,g4)
    c: Equal(g0,g1)
    c: Parallel(g1,g3)
    c: Parallel(g2,g0)
    c: Perpendicular(g1,g0)
    c: Distance(g1) = 14.1
    c: Coincident(g5,g6)
    c: Coincident(g6,g7)
    c: Coincident(g7,g8)
    c: Coincident(g8,g5)
    c: Symmetric(g7,g5,g9)
    c: Equal(g5,g6)
    c: Parallel(g5,g7)
    c: Parallel(g6,g8)
    c: Perpendicular(g5,g6)
    c: Parallel(g6,g1)
    c: Coincident(g10,g4)
    c: Coincident(g10,g9)
    c: Perpendicular(g2,g10)
    c: Equal(g1,g6)
    c: Distance(g10) = 19.05
    c: Coincident(g11,g12)
    c: Coincident(g12,g13)
    c: Coincident(g13,g14)
    c: Coincident(g14,g11)
    c: Symmetric(g13,g11,g15)
    c: Parallel(g13,g11)
    c: Parallel(g12,g14)
    c: Perpendicular(g12,g11)
    c: Equal(g12,g3)
    c: Equal(g12,g11)
    c: PointOnObject(g16,g10)
    c: Coincident(g16,g15)
    c: Perpendicular(g10,g16)
    c: Perpendicular(g12,g16)
    c: Angle(g10,g-1) = 0.785398
    c: Coincident(g17,g7)
    c: Coincident(g17,g12)
    c: Coincident(g18,g11)
    c: Coincident(g18,g0)
    c: Equal(g18,g17)
    c: DistanceX(g7,g-3) = 22
    c: DistanceY(g7,g-3) = 9.97038
    c: Block(g10)
    c: Distance(g16) = 25
FEATURE [PartDesign::Pocket] Pocket020
  BaseFeature = -> BaseFeature002
  Direction = (0,0,-1)
  Length = 5
  Length2 = 5
  Profile = -> Sketch029
  ReferenceAxis = -> Sketch029 [N_Axis]
  Type = 1
FEATURE [Sketcher::SketchObject] Sketch030
  AttachmentOffset = pos=(0,0,1.3) rot=(0,0,1;0rad)
  ExternalGeometry = -> [Pocket020]
  FullyConstrained = true
  MapMode = 5
  Placement = pos=(0,0,1.3) rot=(0,0,1;0rad)
  Support = -> [XY_Plane013]
  expr: .AttachmentOffset.Base.z = Spreadsheet.h_plate
  sketch-geometry (20):
    g0: LineSegment StartX=101.875 StartY=160 StartZ=0 EndX=101.875 EndY=268.536 EndZ=0
    g1: LineSegment StartX=101.875 StartY=268.536 StartZ=0 EndX=180.166 EndY=295.713 EndZ=0
    g2: LineSegment StartX=180.166 StartY=295.713 StartZ=0 EndX=335.212 EndY=273.3 EndZ=0
    g3: LineSegment StartX=335.212 StartY=273.3 StartZ=0 EndX=335.212 EndY=160 EndZ=0
    g4: LineSegment StartX=335.212 StartY=160 StartZ=0 EndX=101.875 EndY=160 EndZ=0
    g5: LineSegment StartX=116.675 StartY=222.5 StartZ=0 EndX=116.675 EndY=166 EndZ=0
    g6: LineSegment StartX=116.675 StartY=166 StartZ=0 EndX=113.875 EndY=166 EndZ=0
    g7: LineSegment StartX=113.875 StartY=166 StartZ=0 EndX=113.875 EndY=222.5 EndZ=0
    g8: LineSegment StartX=113.875 StartY=222.5 StartZ=0 EndX=116.675 EndY=222.5 EndZ=0
    g9: GeomPoint X=115.275 Y=194.25 Z=0
    g10: LineSegment StartX=139.525 StartY=222.5 StartZ=0 EndX=139.525 EndY=166 EndZ=0
    g11: LineSegment StartX=139.525 StartY=166 StartZ=0 EndX=136.725 EndY=166 EndZ=0
    g12: LineSegment StartX=136.725 StartY=166 StartZ=0 EndX=136.725 EndY=222.5 EndZ=0
    g13: LineSegment StartX=136.725 StartY=222.5 StartZ=0 EndX=139.525 EndY=222.5 EndZ=0
    g14: GeomPoint X=138.125 Y=194.25 Z=0
    g15: LineSegment StartX=155.753 StartY=278.77 StartZ=0 EndX=153.13 EndY=286.328 EndZ=0
    g16: LineSegment StartX=0 StartY=0 StartZ=0 EndX=600 EndY=0 EndZ=0
    g17: LineSegment StartX=600 StartY=0 StartZ=0 EndX=600 EndY=600 EndZ=0
    g18: LineSegment StartX=600 StartY=600 StartZ=0 EndX=0 EndY=600 EndZ=0
    g19: LineSegment StartX=0 StartY=600 StartZ=0 EndX=0 EndY=0 EndZ=0
  constraints (59):
    c: Coincident(g0,g1)
    c: Coincident(g1,g2)
    c: Coincident(g2,g3)
    c: Vertical(g3)
    c: Coincident(g3,g4)
    c: Coincident(g4,g0)
    c: Horizontal(g4)
    c: Coincident(g5,g6)
    c: Coincident(g6,g7)
    c: Coincident(g7,g8)
    c: Coincident(g8,g5)
    c: Vertical(g5)
    c: Vertical(g7)
    c: Horizontal(g6)
    c: Horizontal(g8)
    c: Symmetric(g7,g5,g9)
    c: Coincident(g10,g11)
    c: Coincident(g11,g12)
    c: Coincident(g12,g13)
    c: Coincident(g13,g10)
    c: Vertical(g10)
    c: Vertical(g12)
    c: Horizontal(g11)
    c: Horizontal(g13)
    c: Symmetric(g12,g10,g14)
    c: DistanceX(g9,g14) = 22.85
    c: PointOnObject(g7,g13)
    c: Equal(g7,g10)
    c: Equal(g6,g11)
    c: DistanceX(g8,g8) = 2.8
    c: DistanceY(g7,g7) = 56.5
    c: DistanceY(g3,g-3) = 15
    c: DistanceX(g-3,g3) = 8
    c: DistanceY(g0,g6) = 6
    c: DistanceX(g0,g6) = 12
    c: DistanceY(g-5,g1) = 6
    c: DistanceX(g1,g-5) = 0
    c: Coincident(g15,g-6)
    c: PointOnObject(g15,g1)
    c: Perpendicular(g1,g15)
    c: Distance(g15) = 8
    c: Coincident(g16,g17)
    c: Coincident(g17,g18)
    c: Coincident(g18,g19)
    c: Coincident(g19,g16)
    c: Horizontal(g16)
    c: Horizontal(g18)
    c: Vertical(g17)
    c: Vertical(g19)
    c: Distance(g17,g19) = 600
    c: Distance(g16,g18) = 600
    c: Coincident(g16,g-1)
    c: Block(g3)
    c: Block(g2)
    c: Block(g1)
    c: Block(g12)
    c: Vertical(g0)
    c: DistanceY(g-7,g2) = 8
    c: DistanceX(g10,g-4) = 45
FEATURE [PartDesign::Pocket] Pocket021
  BaseFeature = -> Pocket020
  Direction = (0,0,-1)
  Length = 5
  Length2 = 5
  Profile = -> Sketch030
  ReferenceAxis = -> Sketch030 [N_Axis]
  Type = 1
FEATURE [Sketcher::SketchObject] Sketch031
  AttachmentOffset = pos=(0,0,1.3) rot=(0,0,1;0rad)
  ExternalGeometry = -> [Sketch030]
  FullyConstrained = true
  MapMode = 5
  Placement = pos=(0,0,1.3) rot=(0,0,1;0rad)
  Support = -> [XY_Plane013]
  expr: .AttachmentOffset.Base.z = Spreadsheet.h_plate
  expr: Constraints[39] = Spreadsheet.d_wall_out
  sketch-geometry (16):
    g0: LineSegment StartX=101.875 StartY=160 StartZ=0 EndX=101.875 EndY=268.536 EndZ=0
    g1: LineSegment StartX=101.875 StartY=268.536 StartZ=0 EndX=180.166 EndY=295.713 EndZ=0
    g2: LineSegment StartX=180.166 StartY=295.713 StartZ=0 EndX=335.212 EndY=273.3 EndZ=0
    g3: LineSegment StartX=335.212 StartY=273.3 StartZ=0 EndX=335.212 EndY=160 EndZ=0
    g4: LineSegment StartX=335.212 StartY=160 StartZ=0 EndX=101.875 EndY=160 EndZ=0
    g5: LineSegment StartX=103.875 StartY=162 StartZ=0 EndX=103.875 EndY=267.23 EndZ=0
    g6: LineSegment StartX=103.875 StartY=267.23 StartZ=0 EndX=180.166 EndY=293.713 EndZ=0
    g7: LineSegment StartX=180.166 StartY=293.713 StartZ=0 EndX=333.212 EndY=271.589 EndZ=0
    g8: LineSegment StartX=333.212 StartY=271.589 StartZ=0 EndX=333.212 EndY=162 EndZ=0
    g9: LineSegment StartX=333.212 StartY=162 StartZ=0 EndX=103.875 EndY=162 EndZ=0
    g10: LineSegment StartX=103.875 StartY=162 StartZ=0 EndX=103.875 EndY=160 EndZ=0
    g11: LineSegment StartX=103.875 StartY=162 StartZ=0 EndX=101.875 EndY=162 EndZ=0
    g12: LineSegment StartX=103.875 StartY=267.23 StartZ=0 EndX=101.875 EndY=267.23 EndZ=0
    g13: LineSegment StartX=180.166 StartY=295.713 StartZ=0 EndX=180.166 EndY=293.713 EndZ=0
    g14: LineSegment StartX=333.212 StartY=271.589 StartZ=0 EndX=335.212 EndY=271.589 EndZ=0
    g15: LineSegment StartX=333.212 StartY=162 StartZ=0 EndX=335.212 EndY=162 EndZ=0
  constraints (42):
    c: Coincident(g-4,g0)
    c: Coincident(g0,g-7)
    c: Coincident(g0,g1)
    c: Coincident(g1,g-7)
    c: Coincident(g1,g2)
    c: Coincident(g2,g-6)
    c: Coincident(g2,g3)
    c: Coincident(g3,g-5)
    c: Coincident(g3,g4)
    c: Coincident(g4,g0)
    c: Coincident(g5,g6)
    c: Coincident(g5,g9)
    c: Coincident(g6,g7)
    c: Coincident(g7,g8)
    c: Coincident(g8,g9)
    c: Coincident(g10,g5)
    c: PointOnObject(g10,g4)
    c: Vertical(g10)
    c: Coincident(g11,g5)
    c: PointOnObject(g11,g0)
    c: Horizontal(g11)
    c: Equal(g11,g10)
    c: Coincident(g12,g5)
    c: PointOnObject(g12,g0)
    c: Coincident(g13,g1)
    c: Coincident(g6,g13)
    c: Vertical(g13)
    c: Horizontal(g12)
    c: Coincident(g14,g7)
    c: PointOnObject(g14,g3)
    c: Horizontal(g14)
    c: Parallel(g7,g2)
    c: Coincident(g15,g8)
    c: PointOnObject(g15,g3)
    c: Horizontal(g15)
    c: Equal(g15,g14)
    c: Equal(g14,g13)
    c: Equal(g13,g12)
    c: Equal(g12,g11)
    c: DistanceX(g11,g11) = 2
    c: Horizontal(g9)
    c: Parallel(g6,g1)
FEATURE [PartDesign::Pad] Pad029
  BaseFeature = -> Pocket021
  Direction = (0,0,1)
  Length = 15
  Length2 = 10
  Profile = -> Sketch031
  ReferenceAxis = -> Sketch031 [N_Axis]
  Type = 0
  expr: Length = Spreadsheet.h_wall_out
FEATURE [PartDesign::Pad] Pad030
  BaseFeature = -> Pad029
  Direction = (0,0,1)
  Length = 10
  Length2 = 10
  Profile = -> Sketch032
  ReferenceAxis = -> Sketch032 [N_Axis]
  Type = 3
  UpToFace = -> Pad029 [Face161]
FEATURE [PartDesign::LinearPattern] LinearPattern001
  BaseFeature = -> Pad030
  Direction = -> Y_Axis013
  Length = 57.15
  Mode = 1
  Occurrences = 4
  Offset = 19.05
  Originals = -> [Pad030]
  expr: Offset = Spreadsheet.d_key
FEATURE [PartDesign::Pad] Pad031
  BaseFeature = -> LinearPattern001
  Direction = (-1,0,0)
  Length = 2
  Length2 = 10
  Profile = -> LinearPattern001 [Face167]
  Type = 0
  expr: Length = Spreadsheet.d_wall_out
FEATURE [PartDesign::Pad] Pad032
  BaseFeature = -> Pad031
  Direction = (0,-1,0)
  Length = 10
  Length2 = 10
  Profile = -> Pad031 [Face169]
  Type = 2
FEATURE [Sketcher::SketchObject] Sketch033
  AttachmentOffset = pos=(0,0,1.5) rot=(0,0,1;0rad)
  ExternalGeometry = -> [Pad032]
  FullyConstrained = true
  MapMode = 5
  Placement = pos=(0,0,1.5) rot=(0,0,1;0rad)
  Support = -> [XY_Plane013]
  expr: .AttachmentOffset.Base.z = Spreadsheet.h_plate
  expr: Constraints[11] = Spreadsheet.d_wall_out
  expr: Constraints[25] = Spreadsheet.d_wall_out
  sketch-geometry (10):
    g0: LineSegment StartX=178.212 StartY=230.45 StartZ=0 EndX=103.875 EndY=267.23 EndZ=0
    g1: LineSegment StartX=103.875 StartY=267.23 StartZ=0 EndX=103.875 EndY=264.999 EndZ=0
    g2: LineSegment StartX=103.875 StartY=264.999 StartZ=0 EndX=178.212 EndY=228.219 EndZ=0
    g3: LineSegment StartX=178.212 StartY=228.219 StartZ=0 EndX=178.212 EndY=230.45 EndZ=0
    g4: LineSegment StartX=178.212 StartY=230.45 StartZ=0 EndX=177.326 EndY=228.657 EndZ=0
    g5: LineSegment StartX=176.212 StartY=249.5 StartZ=0 EndX=215.014 EndY=288.675 EndZ=0
    g6: LineSegment StartX=215.014 StartY=288.675 StartZ=0 EndX=217.8 EndY=288.273 EndZ=0
    g7: LineSegment StartX=217.8 StartY=288.273 StartZ=0 EndX=179.027 EndY=249.5 EndZ=0
    g8: LineSegment StartX=179.027 StartY=249.5 StartZ=0 EndX=176.212 EndY=249.5 EndZ=0
    g9: LineSegment StartX=179.027 StartY=249.5 StartZ=0 EndX=177.606 EndY=250.907 EndZ=0
  constraints (27):
    c: Coincident(g-3,g0)
    c: Coincident(g0,g-4)
    c: Coincident(g0,g1)
    c: Vertical(g1)
    c: Coincident(g1,g2)
    c: Coincident(g2,g3)
    c: Coincident(g3,g0)
    c: Vertical(g3)
    c: Coincident(g4,g0)
    c: PointOnObject(g4,g2)
    c: Perpendicular(g2,g4)
    c: Distance(g4) = 2
    c: Equal(g1,g3)
    c: Coincident(g-5,g5)
    c: PointOnObject(g5,g-6)
    c: Coincident(g5,g6)
    c: PointOnObject(g6,g-6)
    c: Coincident(g6,g7)
    c: PointOnObject(g7,g-5)
    c: Coincident(g7,g8)
    c: Coincident(g8,g5)
    c: Equal(g8,g6)
    c: Coincident(g9,g7)
    c: PointOnObject(g9,g5)
    c: Perpendicular(g5,g9)
    c: Distance(g9) = 2
    c: Angle(g-1,g7) = 0.785398
FEATURE [PartDesign::Pad] Pad033
  BaseFeature = -> Pad032
  Direction = (0,0,1)
  Length = 8
  Length2 = 10
  Profile = -> Sketch033
  ReferenceAxis = -> Sketch033 [N_Axis]
  Type = 0
  expr: Length = Spreadsheet.h_wall_in
FEATURE [PartDesign::Pocket] Pocket022
  BaseFeature = -> Pad033
  Direction = (0,0,-1)
  Length = 0
  Length2 = 5
  Profile = -> Pad033 [Face201]
  Type = 3
  UpToFace = -> Pad033 [Face202]
FEATURE [PartDesign::Body] Body003  label="plate_right_v2"
  BaseFeature = -> baseplate_right_v004_solid
  Group = -> [BaseFeature002,Sketch029,Pocket020,Sketch030,Pocket021,Sketch031,Pad029,Sketch032,Pad030,LinearPattern001,Pad031,Pad032,Sketch033,Pad033,Pocket022]
  Origin = -> Origin013
  Tip = -> Pocket022
FEATURE [App::Part] switch_plate
  Group = -> [LCS_0003,baseplate_left,Body_3,baseplate_left001,baseplate_left001001,baseplate_left001001_solid,plate_right,baseplate_right,baseplate_right001001,baseplate_right001,baseplate_right001001_solid,Body003,baseplate_right_v004_solid001,baseplate_right_v004_solid]
  Origin = -> Origin011
FEATURE [App::DocumentObjectGroup] Parts
  Group = -> [Part_1,Part_2,switch_plate]
